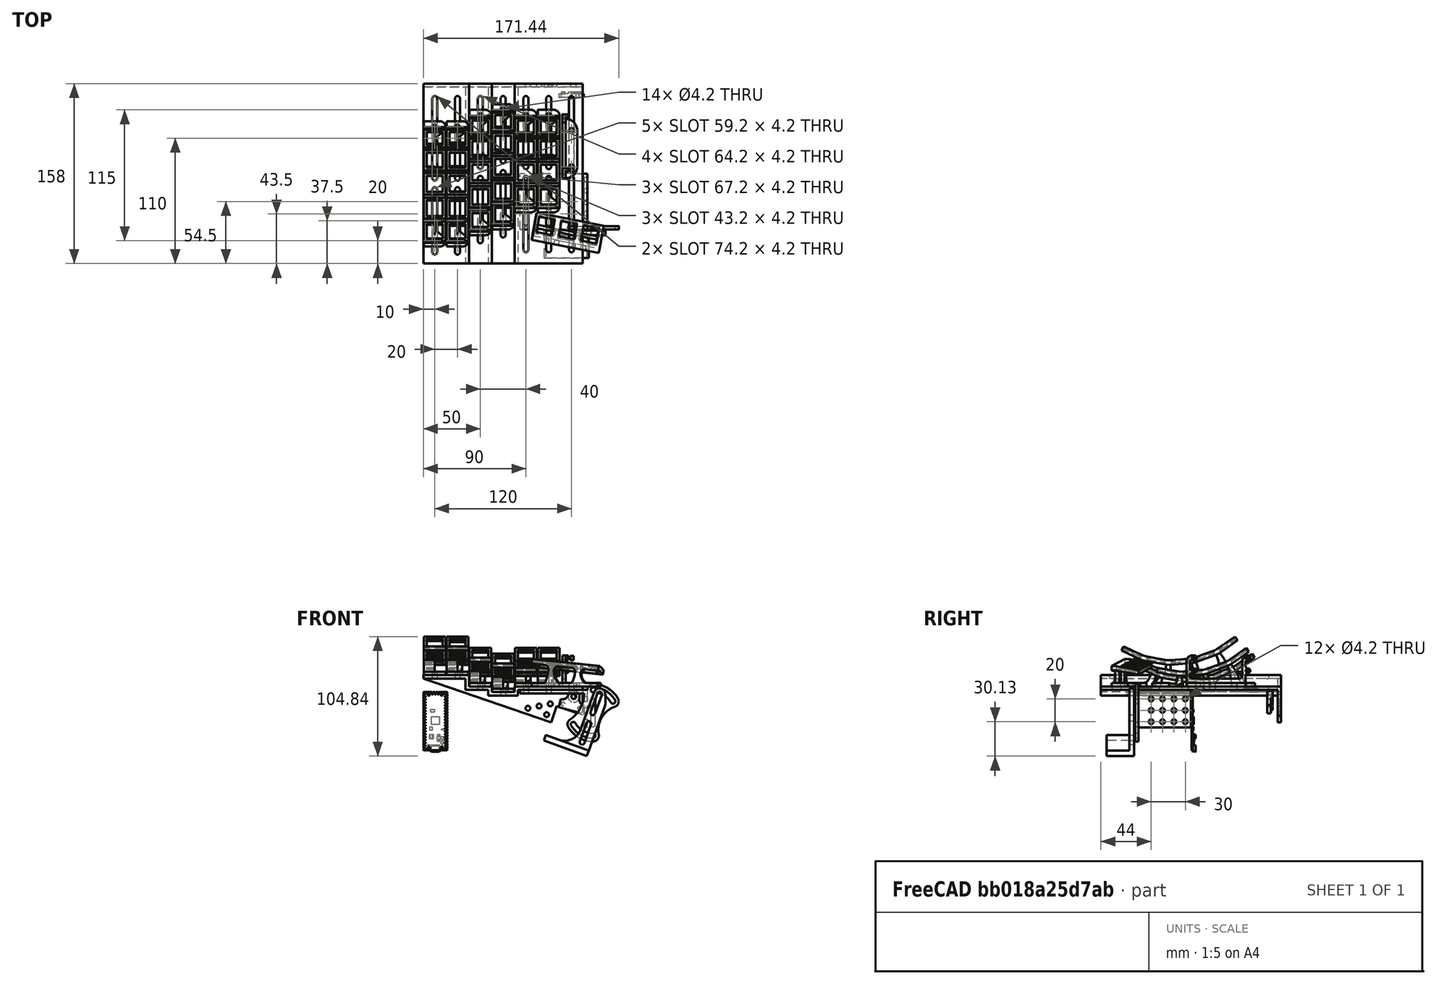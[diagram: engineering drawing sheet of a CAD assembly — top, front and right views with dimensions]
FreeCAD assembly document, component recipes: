
FREECAD ASSEMBLY — COMPONENT RECIPES ("Dactyl Chimera V3")

This assembly document has 15 components, labeled P0..P14 below (a component is one placed body or linked part). 14 of them carry a construction recipe — the FreeCAD feature program that regenerates the part from scratch, quoted from this document or its linked companion documents; the rest are supplied as boundary geometry only. No exploded tour is included for this assembly.
NOTE — this tour is split across 4 documents so each fits a 32k-token context. This is document 1: the component sections continue in the remaining 3 documents, each repeating the header above.
COMPONENT P0 — recipe-attached ("OuterArch", modeled in this document).
Construction recipe (the document's own serialized feature program — sketch geometry with constraints, then the solid features built on it; lengths are millimeters unless a unit is written):

FEATURE [Sketcher::SketchObject] Sketch
  FullyConstrained = true
  MapMode = 5
  Placement = pos=(0,0,0) rot=(0.57735,0.57735,0.57735;2.0944rad)
  Support = -> [YZ_Plane]
  expr: Constraints[147] = <<Spreadsheet>>.ARowKey
  expr: Constraints[148] = <<Spreadsheet>>.ZRowKey
  expr: Constraints[155] = <<Spreadsheet>>.QRowKey
  expr: Constraints[159] = <<Spreadsheet>>.ModRowKey
  expr: Constraints[165] = <<Spreadsheet>>.TopRowKey
  expr: Constraints[171] = <<Spreadsheet>>.Wiring
  sketch-geometry (61):
    g0: LineSegment StartX=-50 StartY=9 StartZ=0 EndX=-50 EndY=3 EndZ=0
    g1: LineSegment StartX=-9.46385 StartY=12.9848 StartZ=0 EndX=0 EndY=13.8128 EndZ=0
    g2: LineSegment StartX=0 StartY=13.8128 StartZ=0 EndX=9.46385 EndY=14.6407 EndZ=0
    g3: LineSegment StartX=9.46385 StartY=14.6407 StartZ=0 EndX=11.8732 EndY=15.1749 EndZ=0
    g4: LineSegment StartX=11.8732 StartY=15.1749 StartZ=0 EndX=20.8002 EndY=18.4241 EndZ=0
    g5: LineSegment StartX=20.8002 StartY=18.4241 StartZ=0 EndX=29.7273 EndY=21.6733 EndZ=0
    g6: LineSegment StartX=29.7273 StartY=21.6733 StartZ=0 EndX=31.9163 EndY=22.8128 EndZ=0
    g7: LineSegment StartX=31.9163 StartY=22.8128 StartZ=0 EndX=39.6982 EndY=28.2617 EndZ=0
    g8: LineSegment StartX=39.6982 StartY=28.2617 StartZ=0 EndX=47.4802 EndY=33.7107 EndZ=0
    g9: LineSegment StartX=47.4802 StartY=33.7107 StartZ=0 EndX=49.7745 EndY=30.4341 EndZ=0
    g10: LineSegment StartX=49.7745 StartY=30.4341 StartZ=0 EndX=34.2106 EndY=19.5362 EndZ=0
    g11: LineSegment StartX=34.2106 StartY=19.5362 StartZ=0 EndX=31.0954 EndY=17.9145 EndZ=0
    g12: LineSegment StartX=31.0954 StartY=17.9145 StartZ=0 EndX=13.2412 EndY=11.4161 EndZ=0
    g13: LineSegment StartX=13.2412 StartY=11.4161 StartZ=0 EndX=9.81247 EndY=10.656 EndZ=0
    g14: LineSegment StartX=9.81247 StartY=10.656 StartZ=0 EndX=-9.11523 EndY=9 EndZ=0
    g15: LineSegment StartX=-9.11523 StartY=9 StartZ=0 EndX=-12.6239 EndY=9.15319 EndZ=0
    g16: LineSegment StartX=-12.6239 StartY=9.15319 StartZ=0 EndX=-31.3353 EndY=12.4525 EndZ=0
    g17: LineSegment StartX=-31.3353 StartY=12.4525 StartZ=0 EndX=-34.6847 EndY=13.5086 EndZ=0
    g18: LineSegment StartX=-34.6847 StartY=13.5086 StartZ=0 EndX=-51.9046 EndY=21.5383 EndZ=0
    g19: LineSegment StartX=-51.9046 StartY=21.5383 StartZ=0 EndX=-50.2141 EndY=25.1636 EndZ=0
    g20: LineSegment StartX=-50.2141 StartY=25.1636 StartZ=0 EndX=-41.6042 EndY=21.1487 EndZ=0
    g21: LineSegment StartX=-41.6042 StartY=21.1487 StartZ=0 EndX=-32.9942 EndY=17.1338 EndZ=0
    g22: LineSegment StartX=-32.9942 StartY=17.1338 StartZ=0 EndX=-30.6407 EndY=16.3917 EndZ=0
    g23: LineSegment StartX=-30.6407 StartY=16.3917 StartZ=0 EndX=-21.285 EndY=14.7421 EndZ=0
    g24: LineSegment StartX=-21.285 StartY=14.7421 StartZ=0 EndX=-11.9293 EndY=13.0924 EndZ=0
    g25: LineSegment StartX=-11.9293 StartY=13.0924 StartZ=0 EndX=-9.46385 EndY=12.9848 EndZ=0
    g26: LineSegment StartX=-34.6847 StartY=13.5086 StartZ=0 EndX=-32.9942 EndY=17.1338 EndZ=0
    g27: LineSegment StartX=-30.6407 StartY=16.3917 StartZ=0 EndX=-31.3353 EndY=12.4525 EndZ=0
    g28: LineSegment StartX=-12.6239 StartY=9.15319 StartZ=0 EndX=-11.9293 EndY=13.0924 EndZ=0
    g29: LineSegment StartX=-9.46385 StartY=12.9848 StartZ=0 EndX=-9.11523 EndY=9 EndZ=0
    g30: LineSegment StartX=9.46385 StartY=14.6407 StartZ=0 EndX=9.81247 EndY=10.656 EndZ=0
    g31: LineSegment StartX=11.8732 StartY=15.1749 StartZ=0 EndX=13.2412 EndY=11.4161 EndZ=0
    g32: LineSegment StartX=29.7273 StartY=21.6733 StartZ=0 EndX=31.0954 EndY=17.9145 EndZ=0
    g33: LineSegment StartX=31.9163 StartY=22.8128 StartZ=0 EndX=34.2106 EndY=19.5362 EndZ=0
    g34: LineSegment StartX=-41.6042 StartY=21.1487 StartZ=0 EndX=-39.4911 EndY=25.6802 EndZ=0
    g35: LineSegment StartX=-21.285 StartY=14.7421 StartZ=0 EndX=-20.4167 EndY=19.6661 EndZ=0
    g36: LineSegment StartX=0 StartY=13.8128 StartZ=0 EndX=-0.435779 EndY=18.7937 EndZ=0
    g37: LineSegment StartX=20.8002 StartY=18.4241 StartZ=0 EndX=19.0901 EndY=23.1225 EndZ=0
    g38: LineSegment StartX=39.6982 StartY=28.2617 StartZ=0 EndX=36.8304 EndY=32.3575 EndZ=0
    g39: LineSegment StartX=-39.4911 StartY=25.6802 StartZ=0 EndX=-36.7722 EndY=24.4124 EndZ=0
    g40: LineSegment StartX=-36.7722 StartY=24.4124 StartZ=0 EndX=-32.546 EndY=33.4755 EndZ=0
    g41: LineSegment StartX=-21.6347 StartY=30.0351 StartZ=0 EndX=-23.3712 EndY=20.1871 EndZ=0
    g42: LineSegment StartX=-23.3712 StartY=20.1871 StartZ=0 EndX=-20.4167 EndY=19.6661 EndZ=0
    g43: LineSegment StartX=-20.4167 StartY=19.6661 StartZ=0 EndX=-17.4623 EndY=19.1452 EndZ=0
    g44: LineSegment StartX=-17.4623 StartY=19.1452 StartZ=0 EndX=-15.7258 EndY=28.9933 EndZ=0
    g45: LineSegment StartX=-4.29592 StartY=28.4942 StartZ=0 EndX=-3.42436 EndY=18.5323 EndZ=0
    g46: LineSegment StartX=-3.42436 StartY=18.5323 StartZ=0 EndX=-0.435779 EndY=18.7937 EndZ=0
    g47: LineSegment StartX=-0.435779 StartY=18.7937 StartZ=0 EndX=2.55281 EndY=19.0552 EndZ=0
    g48: LineSegment StartX=2.55281 StartY=19.0552 StartZ=0 EndX=1.68125 EndY=29.0171 EndZ=0
    g49: LineSegment StartX=12.8509 StartY=31.4934 StartZ=0 EndX=16.2711 EndY=22.0965 EndZ=0
    g50: LineSegment StartX=16.2711 StartY=22.0965 StartZ=0 EndX=19.0901 EndY=23.1225 EndZ=0
    g51: LineSegment StartX=19.0901 StartY=23.1225 StartZ=0 EndX=21.9092 EndY=24.1486 EndZ=0
    g52: LineSegment StartX=21.9092 StartY=24.1486 StartZ=0 EndX=18.489 EndY=33.5455 EndZ=0
    g53: LineSegment StartX=28.6371 StartY=38.8283 StartZ=0 EndX=34.3729 EndY=30.6368 EndZ=0
    g54: LineSegment StartX=34.3729 StartY=30.6368 StartZ=0 EndX=36.8304 EndY=32.3575 EndZ=0
    g55: ArcOfCircle CenterX=-14.0244 CenterY=73.195 CenterZ=0 NormalX=0 NormalY=0 NormalZ=1 AngleXU=0 Radius=43.8257 StartAngle=4.27606 EndAngle=4.53786
    g56: ArcOfCircle CenterX=-8.11558 CenterY=72.1532 CenterZ=0 NormalX=0 NormalY=0 NormalZ=1 AngleXU=0 Radius=43.8257 StartAngle=4.53786 EndAngle=4.79966
    g57: ArcOfCircle CenterX=-2.13841 CenterY=72.6761 CenterZ=0 NormalX=0 NormalY=0 NormalZ=1 AngleXU=0 Radius=43.8257 StartAngle=4.79966 EndAngle=5.06145
    g58: ArcOfCircle CenterX=3.49974 CenterY=74.7282 CenterZ=0 NormalX=0 NormalY=0 NormalZ=1 AngleXU=0 Radius=43.8257 StartAngle=5.06145 EndAngle=5.32325
    g59: LineSegment StartX=-50 StartY=9 StartZ=0 EndX=-70 EndY=9 EndZ=0
    g60: LineSegment StartX=-50 StartY=9 StartZ=0 EndX=50 EndY=9 EndZ=0
  constraints (176):
    c: Vertical(g0)
    c: Coincident(g1,g2)
    c: Coincident(g2,g3)
    c: Coincident(g3,g4)
    c: Coincident(g4,g5)
    c: Coincident(g5,g6)
    c: Coincident(g6,g7)
    c: Coincident(g7,g8)
    c: Coincident(g8,g9)
    c: Coincident(g9,g10)
    c: Coincident(g10,g11)
    c: Coincident(g11,g12)
    c: Coincident(g12,g13)
    c: Coincident(g13,g14)
    c: Coincident(g14,g15)
    c: Coincident(g15,g16)
    c: Coincident(g16,g17)
    c: Coincident(g17,g18)
    c: Coincident(g18,g19)
    c: Coincident(g19,g20)
    c: Coincident(g20,g21)
    c: Coincident(g21,g22)
    c: Coincident(g22,g23)
    c: Coincident(g23,g24)
    c: Coincident(g24,g25)
    c: Coincident(g25,g1)
    c: Coincident(g26,g17)
    c: Coincident(g26,g21)
    c: Coincident(g27,g22)
    c: Coincident(g27,g16)
    c: Coincident(g28,g15)
    c: Coincident(g28,g24)
    c: Coincident(g29,g1)
    c: Coincident(g29,g14)
    c: Coincident(g30,g2)
    c: Coincident(g30,g13)
    c: Coincident(g31,g3)
    c: Coincident(g31,g12)
    c: Coincident(g32,g5)
    c: Coincident(g32,g11)
    c: Coincident(g33,g6)
    c: Coincident(g33,g10)
    c: Coincident(g34,g20)
    c: Coincident(g35,g23)
    c: Coincident(g36,g1)
    c: Coincident(g37,g4)
    c: Coincident(g38,g7)
    c: Parallel(g1,g2)
    c: Parallel(g4,g5)
    c: Parallel(g8,g7)
    c: Parallel(g21,g20)
    c: Parallel(g23,g24)
    c: Equal(g5,g4)
    c: Equal(g7,g8)
    c: Equal(g2,g1)
    c: Equal(g24,g23)
    c: Equal(g21,g20)
    c: Equal(g14,g16)
    c: Equal(g14,g12)
    c: Equal(g14,g10)
    c: Equal(g14,g18)
    c: Perpendicular(g26,g21)
    c: Perpendicular(g18,g26)
    c: Perpendicular(g19,g18)
    c: Perpendicular(g28,g24)
    c: Perpendicular(g16,g28)
    c: Perpendicular(g27,g16)
    c: Perpendicular(g14,g30)
    c: Perpendicular(g29,g14)
    c: Perpendicular(g31,g4)
    c: Perpendicular(g12,g31)
    c: Perpendicular(g32,g12)
    c: Perpendicular(g33,g7)
    c: Perpendicular(g10,g33)
    c: Perpendicular(g9,g10)
    c: Perpendicular(g8,g38)
    c: Perpendicular(g5,g37)
    c: Perpendicular(g1,g36)
    c: Perpendicular(g23,g35)
    c: Perpendicular(g20,g34)
    c: Equal(g29,g28)
    c: Equal(g27,g26)
    c: Equal(g30,g31)
    c: Equal(g32,g33)
    c: Coincident(g39,g40)
    c: Coincident(g41,g42)
    c: Coincident(g42,g35)
    c: Coincident(g42,g43)
    c: Coincident(g43,g44)
    c: Coincident(g45,g46)
    c: Coincident(g46,g36)
    c: Coincident(g46,g47)
    c: Coincident(g47,g48)
    c: Coincident(g49,g50)
    c: Coincident(g50,g37)
    c: Coincident(g50,g51)
    c: Coincident(g51,g52)
    c: Coincident(g53,g54)
    c: Coincident(g54,g38)
    c: Perpendicular(g54,g53)
    c: Perpendicular(g38,g54)
    c: Perpendicular(g51,g52)
    c: Perpendicular(g37,g51)
    c: Perpendicular(g50,g37)
    c: Perpendicular(g49,g50)
    c: Perpendicular(g47,g48)
    c: Perpendicular(g36,g47)
    c: Perpendicular(g46,g36)
    c: Perpendicular(g45,g46)
    c: Perpendicular(g43,g44)
    c: Perpendicular(g35,g43)
    c: Perpendicular(g42,g35)
    c: Perpendicular(g41,g42)
    c: Perpendicular(g39,g40)
    c: Perpendicular(g34,g39)
    c: Coincident(g55,g41)
    c: Coincident(g55,g40)
    c: Coincident(g56,g44)
    c: Coincident(g56,g45)
    c: Coincident(g57,g48)
    c: Coincident(g57,g49)
    c: Coincident(g58,g52)
    c: Coincident(g58,g53)
    c: Equal(g46,g47)
    c: Equal(g47,g50)
    c: Equal(g50,g51)
    c: Equal(g51,g54)
    c: Equal(g39,g42)
    c: Equal(g42,g43)
    c: Equal(g43,g46)
    c: Coincident(g39,g34)
    c: Distance(g14) = 19
    c: Distance(g35,g36) = 20
    c: Perpendicular(g56,g44)
    c: Perpendicular(g57,g48)
    c: Perpendicular(g57,g49)
    c: Angle(g35,g36) = 0.261799
    c: Perpendicular(g56,g45)
    c: Perpendicular(g58,g53)
    c: Perpendicular(g58,g52)
    c: Perpendicular(g55,g41)
    c: Perpendicular(g55,g40)
    c: Distance(g44) = 10
    c: Distance(g45) = 10
    c: Coincident(g59,g0)
    c: Horizontal(g59)
    c: Angle(g59,g36) = 1.65806
    c: Distance(g36) = 5
    c: Distance(g35) = 5
    c: Distance(g41) = 10
    c: Distance(g40) = 10
    c: Distance(g53) = 10
    c: Distance(g52) = 10
    c: Angle(g36,g37) = 0.261799
    c: Distance(g49) = 10
    c: Distance(g37) = 5
    c: Distance(g48) = 10
    c: Distance(g50) = 3
    c: Distance(g37,g36) = 20
    c: Distance(g34) = 5
    c: Angle(g34,g35) = 0.261799
    c: Distance(g35,g34) = 20
    c: Distance(g37,g38) = 20
    c: DistanceX(g0,g-1) = 50
    c: DistanceX(g59,g59) = 20
    c: Distance(g38) = 5
    c: Angle(g37,g38) = 0.261799
    c: Distance(g29) = 4
    c: Equal(g30,g29)
    c: Coincident(g60,g0)
    c: Horizontal(g60)
    c: DistanceY(g0,g0) = 6
    c: DistanceX(g60,g60) = 100
    c: DistanceY(g-1,g0) = 3
    c: PointOnObject(g14,g60)
    c: PointOnObject(g1,g-2)
FEATURE [PartDesign::Pad] Pad  label="OArch"
  Direction = (1,-2e-16,3e-16)
  Length = 19
  Length2 = 100
  Midplane = true
  Placement = pos=(0,0,0) rot=(0.57735,0.57735,0.57735;2.0944rad)
  Profile = -> Sketch
  Type = 0
FEATURE [Sketcher::SketchObject] Sketch001
  ExternalGeometry = -> [Pad]
  FullyConstrained = true
  MapMode = 5
  Placement = pos=(0,0,0) rot=(0.57735,0.57735,0.57735;2.0944rad)
  Support = -> [YZ_Plane]
  expr: Constraints[103] = <<Spreadsheet>>.Wiring
  expr: Constraints[104] = Spreadsheet.Wiring
  expr: Constraints[106] = <<Spreadsheet>>.Wiring
  expr: Constraints[107] = <<Spreadsheet>>.Wiring
  expr: Constraints[108] = <<Spreadsheet>>.Wiring
  expr: Constraints[109] = <<Spreadsheet>>.Wiring
  expr: Constraints[110] = <<Spreadsheet>>.Wiring
  expr: Constraints[111] = <<Spreadsheet>>.ArchLength * 2 - 10mm
  expr: Constraints[21] = <<Spreadsheet>>.ArchLength
  expr: Constraints[34] = <<Spreadsheet>>.ArchLength
  expr: Constraints[8] = <<Spreadsheet>>.Wiring + 4mm
  expr: Constraints[99] = <<Spreadsheet>>.Wiring
  sketch-geometry (44):
    g0: LineSegment StartX=-30.6407 StartY=16.3917 StartZ=0 EndX=-32.9942 EndY=17.1338 EndZ=0
    g1: LineSegment StartX=-11.9293 StartY=13.0924 StartZ=0 EndX=-9.46385 EndY=12.9848 EndZ=0
    g2: LineSegment StartX=11.8732 StartY=15.1749 StartZ=0 EndX=9.46385 EndY=14.6407 EndZ=0
    g3: LineSegment StartX=31.9163 StartY=22.8128 StartZ=0 EndX=29.7273 EndY=21.6733 EndZ=0
    g4: LineSegment StartX=-30.6407 StartY=16.3917 StartZ=0 EndX=-32.3771 EndY=6.54366 EndZ=0
    g5: LineSegment StartX=-11.9293 StartY=13.0924 StartZ=0 EndX=-13.6658 EndY=3.24435 EndZ=0
    g6: LineSegment StartX=-9.46385 StartY=12.9848 StartZ=0 EndX=-8.59229 EndY=3.02283 EndZ=0
    g7: LineSegment StartX=10.3354 StartY=4.67879 StartZ=0 EndX=9.46385 EndY=14.6407 EndZ=0
    g8: LineSegment StartX=11.8732 StartY=15.1749 StartZ=0 EndX=15.2934 EndY=5.77795 EndZ=0
    g9: LineSegment StartX=33.1475 StartY=12.2763 StartZ=0 EndX=29.7273 EndY=21.6733 EndZ=0
    g10: LineSegment StartX=31.9163 StartY=22.8128 StartZ=0 EndX=37.6521 EndY=14.6213 EndZ=0
    g11: LineSegment StartX=-37.2204 StartY=8.07075 StartZ=0 EndX=-32.9942 EndY=17.1338 EndZ=0
    g12: LineSegment StartX=-13.6658 StartY=0 StartZ=0 EndX=-8.59229 EndY=0 EndZ=0
    g13: LineSegment StartX=-45 StartY=3 StartZ=0 EndX=-45 EndY=0 EndZ=0
    g14: LineSegment StartX=-45 StartY=0 StartZ=0 EndX=-35 EndY=0 EndZ=0
    g15: LineSegment StartX=35 StartY=0 StartZ=0 EndX=45 EndY=0 EndZ=0
    g16: LineSegment StartX=45 StartY=3 StartZ=0 EndX=45 EndY=0 EndZ=0
    g17: LineSegment StartX=10.3354 StartY=0 StartZ=0 EndX=15.2934 EndY=0 EndZ=0
    g18: LineSegment StartX=-32.3771 StartY=6.54366 StartZ=0 EndX=-35 EndY=0 EndZ=0
    g19: LineSegment StartX=35 StartY=0 StartZ=0 EndX=33.1475 EndY=12.2763 EndZ=0
    g20-g23: Circle x4 (B-spline internal-alignment scaffolding for g24; pole/knot coordinates omitted)
    g24: BSplineCurve PolesCount=4 KnotsCount=2 Degree=3 IsPeriodic=0
    g25: GeomPoint X=-37.2204 Y=8.07075 Z=0
    g26: GeomPoint X=-45 Y=3 Z=0
    g27-g30: Circle x4 (B-spline internal-alignment scaffolding for g31; pole/knot coordinates omitted)
    g31: BSplineCurve PolesCount=4 KnotsCount=2 Degree=3 IsPeriodic=0
    g32: GeomPoint X=37.6521 Y=14.6213 Z=0
    g33: GeomPoint X=45 Y=3 Z=0
    g34: LineSegment StartX=45 StartY=3 StartZ=0 EndX=40 EndY=3 EndZ=0
    g35: LineSegment StartX=-45 StartY=3 StartZ=0 EndX=-40 EndY=3 EndZ=0
    g36: LineSegment StartX=42.2622 StartY=8.03741 StartZ=0 EndX=37.6521 EndY=14.6213 EndZ=0
    g37: LineSegment StartX=-37.2204 StartY=8.07075 StartZ=0 EndX=-39.0097 EndY=4.23371 EndZ=0
    g38: LineSegment StartX=-39.0097 StartY=0 StartZ=0 EndX=-39.0097 EndY=4.23371 EndZ=0
    g39: LineSegment StartX=42.2622 StartY=8.03741 StartZ=0 EndX=42.2622 EndY=0 EndZ=0
    g40: LineSegment StartX=-13.6658 StartY=3.24435 StartZ=0 EndX=-13.6658 EndY=0 EndZ=0
    g41: LineSegment StartX=-8.59229 StartY=3.02283 StartZ=0 EndX=-8.59229 EndY=0 EndZ=0
    g42: LineSegment StartX=10.3354 StartY=4.67879 StartZ=0 EndX=10.3354 EndY=0 EndZ=0
    g43: LineSegment StartX=15.2934 StartY=5.77795 StartZ=0 EndX=15.2934 EndY=0 EndZ=0
  constraints (107):
    c: Coincident(g-6,g2)
    c: Coincident(g2,g-6)
    c: Coincident(g0,g-10)
    c: Coincident(g0,g-10)
    c: Coincident(g1,g-7)
    c: Coincident(g1,g-7)
    c: Coincident(g-3,g3)
    c: Coincident(g3,g-3)
    c: Distance(g0,g11) = 10
    c: Coincident(g4,g0)
    c: Coincident(g5,g1)
    c: Coincident(g6,g1)
    c: Coincident(g8,g2)
    c: Coincident(g9,g3)
    c: Coincident(g10,g3)
    c: Coincident(g11,g0)
    c: Equal(g11,g4)
    c: Equal(g9,g10)
    c: Coincident(g7,g2)
    c: PointOnObject(g12,g-1)
    c: PointOnObject(g12,g-1)
    c: DistanceX(g-11,g16) = 45
    c: PointOnObject(g13,g-1)
    c: Vertical(g13)
    c: Coincident(g13,g14)
    c: Horizontal(g14)
    c: DistanceY(g13,g13) = 3
    c: PointOnObject(g17,g-1)
    c: Horizontal(g15)
    c: Coincident(g16,g15)
    c: Vertical(g16)
    c: Equal(g13,g16)
    c: PointOnObject(g15,g-1)
    c: Horizontal(g17)
    c: DistanceX(g13,g-11) = 45
    c: Coincident(g18,g4)
    c: Coincident(g18,g14)
    c: Coincident(g19,g15)
    c: Coincident(g19,g9)
    c: Coincident(g24,g11)
    c: Weight(g20) = 1
    c: Equal(g20,g21)
    c: Equal(g20,g22)
    c: Equal(g20,g23)
    c: Coincident(g24,g13)
    c: InternalAlignment(g20-g23 -> g24) x4
    c: InternalAlignment(g25,g24)
    c: InternalAlignment(g26,g24)
    c: Coincident(g31,g10)
    c: Weight(g27) = 1
    c: Equal(g27,g28)
    c: Equal(g27,g29)
    c: Equal(g27,g30)
    c: Coincident(g31,g16)
    c: InternalAlignment(g27-g30 -> g31) x4
    c: InternalAlignment(g32,g31)
    c: InternalAlignment(g33,g31)
    c: Coincident(g34,g29)
    c: Coincident(g35,g13)
    c: Coincident(g35,g22)
    c: Coincident(g36,g28)
    c: Coincident(g36,g10)
    c: Coincident(g37,g11)
    c: Coincident(g37,g21)
    c: PointOnObject(g38,g-1)
    c: Coincident(g38,g21)
    c: Equal(g37,g38)
    c: Parallel(g37,g11)
    c: DistanceX(g35,g35) = 5
    c: Coincident(g34,g16)
    c: Equal(g34,g35)
    c: Coincident(g39,g28)
    c: PointOnObject(g39,g-1)
    c: Equal(g36,g39)
    c: Parallel(g36,g10)
    c: Vertical(g38)
    c: Vertical(g39)
    c: Equal(g15,g14)
    c: DistanceX(g14,g14) = 10
    c: Distance(g10) = 10
    c: Equal(g9,g4)
    c: Coincident(g40,g5)
    c: Coincident(g40,g12)
    c: Coincident(g41,g6)
    c: Coincident(g41,g12)
    c: Vertical(g41)
    c: Vertical(g40)
    c: Coincident(g42,g7)
    c: Coincident(g42,g17)
    c: Coincident(g43,g8)
    c: Coincident(g43,g17)
    c: Vertical(g43)
    c: Vertical(g42)
    c: Distance(g-8,g5) = 6
    c: Equal(g6,g5)
    c: Equal(g5,g7)
    c: Equal(g7,g8)
    c: Distance(g-9,g11) = 6
    c: Distance(g-9,g4) = 6
    c: Equal(g5,g11)
    c: Distance(g-5,g7) = 6
    c: Distance(g-5,g8) = 6
    c: Distance(g-4,g9) = 6
    c: Distance(g10,g-4) = 6
    c: Distance(g6,g-8) = 6
    c: DistanceX(g22,g29) = 80
    c: Horizontal(g35)
FEATURE [PartDesign::Pad] Pad001  label="OLegs"
  BaseFeature = -> Pad
  Direction = (1,-2e-16,3e-16)
  Length = 9.5
  Length2 = 100
  Placement = pos=(0,0,0) rot=(0.57735,0.57735,0.57735;2.0944rad)
  Profile = -> Sketch001
  Reversed = true
  Type = 0
FEATURE [Sketcher::SketchObject] Sketch002
  ExternalGeometry = -> [Sketch001]
  FullyConstrained = true
  MapMode = 5
  Support = -> [XY_Plane]
  expr: Constraints[14] = <<Spreadsheet>>.NutR
  expr: Constraints[15] = <<Spreadsheet>>.NutR
  expr: Constraints[26] = <<Spreadsheet>>.ScrewD
  expr: Constraints[27] = <<Spreadsheet>>.NutR
  expr: Constraints[28] = Spreadsheet.NutR
  expr: Constraints[8] = <<Spreadsheet>>.ScrewD
  sketch-geometry (22):
    g0: LineSegment StartX=-1e-14 StartY=-45 StartZ=0 EndX=-9.5 EndY=-45 EndZ=0
    g1: LineSegment StartX=-9.5 StartY=-45 StartZ=0 EndX=-9.5 EndY=-55 EndZ=0
    g2: LineSegment StartX=-9.5 StartY=-55 StartZ=0 EndX=4.5 EndY=-55 EndZ=0
    g3: LineSegment StartX=-1e-14 StartY=-45 StartZ=0 EndX=-1e-14 EndY=-40 EndZ=0
    g4: Circle CenterX=0 CenterY=-50 CenterZ=0 NormalX=0 NormalY=0 NormalZ=1 AngleXU=0 Radius=2.1
    g5: ArcOfCircle CenterX=4.5 CenterY=-50 CenterZ=0 NormalX=0 NormalY=0 NormalZ=1 AngleXU=0 Radius=5 StartAngle=4.71239 EndAngle=7.17949
    g6: LineSegment StartX=0 StartY=-50 StartZ=0 EndX=4.5 EndY=-50 EndZ=0
    g7: LineSegment StartX=9.8e-15 StartY=40 StartZ=0 EndX=9.8e-15 EndY=45 EndZ=0
    g8: LineSegment StartX=9.8e-15 StartY=45 StartZ=0 EndX=-9.5 EndY=45 EndZ=0
    g9: LineSegment StartX=-9.5 StartY=45 StartZ=0 EndX=-9.5 EndY=55 EndZ=0
    g10: LineSegment StartX=-9.5 StartY=55 StartZ=0 EndX=4.5 EndY=55 EndZ=0
    g11: ArcOfCircle CenterX=4.5 CenterY=50 CenterZ=0 NormalX=0 NormalY=0 NormalZ=1 AngleXU=0 Radius=5 StartAngle=5.38688 EndAngle=7.85398
    g12: Circle CenterX=0 CenterY=50 CenterZ=0 NormalX=0 NormalY=0 NormalZ=1 AngleXU=0 Radius=2.1
    g13: LineSegment StartX=0 StartY=50 StartZ=0 EndX=4.5 EndY=50 EndZ=0
    g14: LineSegment StartX=7.6225 StartY=46.0949 StartZ=0 EndX=9.8e-15 EndY=40 EndZ=0
    g15: LineSegment StartX=-1e-14 StartY=-40 StartZ=0 EndX=7.6225 EndY=-46.0949 EndZ=0
    g16: LineSegment StartX=9.5 StartY=55 StartZ=0 EndX=9.5 EndY=50 EndZ=0
    g17: LineSegment StartX=-9.5 StartY=55 StartZ=0 EndX=0 EndY=50 EndZ=0
    g18: LineSegment StartX=9.5 StartY=55 StartZ=0 EndX=0 EndY=50 EndZ=0
    g19: LineSegment StartX=9.5 StartY=-50 StartZ=0 EndX=9.5 EndY=-55 EndZ=0
    g20: LineSegment StartX=9.5 StartY=-55 StartZ=0 EndX=0 EndY=-50 EndZ=0
    g21: LineSegment StartX=0 StartY=-50 StartZ=0 EndX=-9.5 EndY=-55 EndZ=0
  constraints (58):
    c: Coincident(g0,g-3)
    c: Horizontal(g0)
    c: Coincident(g1,g0)
    c: Vertical(g1)
    c: Coincident(g2,g1)
    c: Horizontal(g2)
    c: Coincident(g3,g0)
    c: DistanceY(g3,g3) = 5
    c: Diameter(g4) = 4.2
    c: Tangent(g5,g2) = -1.5708
    c: Coincident(g6,g4)
    c: Coincident(g6,g5)
    c: Horizontal(g6)
    c: PointOnObject(g4,g-2)
    c: DistanceY(g4,g0) = 5
    c: DistanceY(g1,g4) = 5
    c: Vertical(g7)
    c: Coincident(g7,g8)
    c: Horizontal(g8)
    c: Coincident(g8,g9)
    c: Vertical(g9)
    c: Coincident(g9,g10)
    c: Horizontal(g10)
    c: Tangent(g11,g10) = 1.5708
    c: DistanceY(g7,g7) = 5
    c: PointOnObject(g12,g-2)
    c: Diameter(g12) = 4.2
    c: DistanceY(g8,g12) = 5
    c: DistanceY(g12,g9) = 5
    c: Coincident(g13,g12)
    c: Coincident(g13,g11)
    c: Horizontal(g13)
    c: Coincident(g14,g7)
    c: Vertical(g3)
    c: Coincident(g15,g3)
    c: Coincident(g7,g-4)
    c: Tangent(g14,g11) = 1.5708
    c: Vertical(g16)
    c: Tangent(g16,g11)
    c: PointOnObject(g16,g11)
    c: Horizontal(g16,g10)
    c: DistanceX(g9,g16) = 19
    c: Coincident(g17,g9)
    c: Coincident(g17,g12)
    c: Coincident(g18,g16)
    c: Coincident(g18,g12)
    c: Equal(g18,g17)
    c: Tangent(g15,g5) = 1.5708
    c: Vertical(g19)
    c: Tangent(g19,g5)
    c: Coincident(g19,g20)
    c: Coincident(g20,g4)
    c: Coincident(g20,g21)
    c: Coincident(g21,g1)
    c: Horizontal(g19,g2)
    c: PointOnObject(g19,g5)
    c: Equal(g20,g21)
    c: DistanceX(g1,g19) = 19
FEATURE [PartDesign::Pad] Pad002  label="OFeet"
  BaseFeature = -> Pad001
  Direction = (0,0,1)
  Length = 3
  Length2 = 100
  Placement = pos=(0,0,0) rot=(0.57735,0.57735,0.57735;2.0944rad)
  Profile = -> Sketch002
  Type = 0
FEATURE [Sketcher::SketchObject] Sketch003
  ExternalGeometry = -> [Sketch]
  FullyConstrained = true
  MapMode = 5
  Placement = pos=(0,0,0) rot=(0.57735,0.57735,0.57735;2.0944rad)
  Support = -> [YZ_Plane]
  sketch-geometry (75):
    g0: LineSegment StartX=-41.6042 StartY=21.1487 StartZ=0 EndX=-47.9483 EndY=24.107 EndZ=0
    g1: LineSegment StartX=-41.6042 StartY=21.1487 StartZ=0 EndX=-35.26 EndY=18.1904 EndZ=0
    g2: LineSegment StartX=-41.6042 StartY=21.1487 StartZ=0 EndX=-43.2946 EndY=17.5235 EndZ=0
    g3: LineSegment StartX=-35.7723 StartY=14.0157 StartZ=0 EndX=-43.2946 EndY=17.5235 EndZ=0
    g4: LineSegment StartX=-43.2946 StartY=17.5235 StartZ=0 EndX=-50.817 EndY=21.0312 EndZ=0
    g5: LineSegment StartX=-50.817 StartY=21.0312 StartZ=0 EndX=-49.7182 EndY=23.3876 EndZ=0
    g6: LineSegment StartX=-47.9483 StartY=24.107 StartZ=0 EndX=-49.6388 EndY=20.4818 EndZ=0
    g7: LineSegment StartX=-49.7182 StartY=23.3876 StartZ=0 EndX=-48.54 EndY=22.8382 EndZ=0
    g8: LineSegment StartX=-48.54 StartY=22.8382 StartZ=0 EndX=-47.9483 EndY=24.107 EndZ=0
    g9: LineSegment StartX=-35.26 StartY=18.1904 StartZ=0 EndX=-35.8517 EndY=16.9215 EndZ=0
    g10: LineSegment StartX=-35.8517 StartY=16.9215 StartZ=0 EndX=-34.6735 EndY=16.3721 EndZ=0
    g11: LineSegment StartX=-35.7723 StartY=14.0157 StartZ=0 EndX=-34.6735 EndY=16.3721 EndZ=0
    g12: LineSegment StartX=-35.26 StartY=18.1904 StartZ=0 EndX=-36.9505 EndY=14.5651 EndZ=0
    g13: LineSegment StartX=-35.7723 StartY=14.0157 StartZ=0 EndX=-34.0818 EndY=17.641 EndZ=0
    g14: LineSegment StartX=-21.285 StartY=14.7421 StartZ=0 EndX=-21.9796 EndY=10.8028 EndZ=0
    g15: LineSegment StartX=0 StartY=13.8128 StartZ=0 EndX=0.348623 EndY=9.82798 EndZ=0
    g16: LineSegment StartX=20.8002 StartY=18.4241 StartZ=0 EndX=22.1683 EndY=14.6653 EndZ=0
    g17: LineSegment StartX=39.6982 StartY=28.2617 StartZ=0 EndX=41.9925 EndY=24.9851 EndZ=0
    g18: LineSegment StartX=-28.1786 StartY=15.9576 StartZ=0 EndX=-21.285 EndY=14.7421 EndZ=0
    g19: LineSegment StartX=-21.285 StartY=14.7421 StartZ=0 EndX=-14.3913 EndY=13.5265 EndZ=0
    g20: LineSegment StartX=-6.97336 StartY=13.2027 StartZ=0 EndX=0 EndY=13.8128 EndZ=0
    g21: LineSegment StartX=0 StartY=13.8128 StartZ=0 EndX=6.97336 EndY=14.4228 EndZ=0
    g22: LineSegment StartX=14.2224 StartY=16.0299 StartZ=0 EndX=20.8002 EndY=18.4241 EndZ=0
    g23: LineSegment StartX=20.8002 StartY=18.4241 StartZ=0 EndX=27.3781 EndY=20.8182 EndZ=0
    g24: LineSegment StartX=33.9642 StartY=24.2467 StartZ=0 EndX=39.6982 EndY=28.2617 EndZ=0
    g25: LineSegment StartX=39.6982 StartY=28.2617 StartZ=0 EndX=45.4323 EndY=32.2768 EndZ=0
    g26: LineSegment StartX=-30.1535 StartY=12.2441 StartZ=0 EndX=-21.9796 EndY=10.8028 EndZ=0
    g27: LineSegment StartX=-21.9796 StartY=10.8028 StartZ=0 EndX=-13.8057 EndY=9.36157 EndZ=0
    g28: LineSegment StartX=-7.91979 StartY=9.10459 StartZ=0 EndX=0.348623 EndY=9.82798 EndZ=0
    g29: LineSegment StartX=0.348623 StartY=9.82798 StartZ=0 EndX=8.61704 EndY=10.5514 EndZ=0
    g30: LineSegment StartX=14.3689 StartY=11.8265 StartZ=0 EndX=22.1683 EndY=14.6653 EndZ=0
    g31: LineSegment StartX=22.1683 StartY=14.6653 StartZ=0 EndX=29.9678 EndY=17.5041 EndZ=0
    g32: LineSegment StartX=-28.1786 StartY=15.9576 StartZ=0 EndX=-28.8732 EndY=12.0184 EndZ=0
    g33: LineSegment StartX=-14.3913 StartY=13.5265 StartZ=0 EndX=-15.0859 EndY=9.58731 EndZ=0
    g34: LineSegment StartX=-13.8057 StartY=9.36157 StartZ=0 EndX=-13.1111 EndY=13.3008 EndZ=0
    g35: LineSegment StartX=-6.97336 StartY=13.2027 StartZ=0 EndX=-6.62474 EndY=9.21789 EndZ=0
    g36: LineSegment StartX=-7.91979 StartY=9.10459 StartZ=0 EndX=-8.26842 EndY=13.0894 EndZ=0
    g37: LineSegment StartX=6.97336 StartY=14.4228 StartZ=0 EndX=7.32199 EndY=10.4381 EndZ=0
    g38: LineSegment StartX=8.61704 StartY=10.5514 StartZ=0 EndX=8.26842 EndY=14.5362 EndZ=0
    g39: LineSegment StartX=14.3689 StartY=11.8265 StartZ=0 EndX=13.0008 EndY=15.5853 EndZ=0
    g40: LineSegment StartX=14.2224 StartY=16.0299 StartZ=0 EndX=15.5905 EndY=12.2711 EndZ=0
    g41: LineSegment StartX=27.3781 StartY=20.8182 StartZ=0 EndX=28.7462 EndY=17.0594 EndZ=0
    g42: LineSegment StartX=29.9678 StartY=17.5041 StartZ=0 EndX=28.5997 EndY=21.2628 EndZ=0
    g43: LineSegment StartX=35.1936 StartY=20.2244 StartZ=0 EndX=32.8993 EndY=23.5011 EndZ=0
    g44: LineSegment StartX=33.9642 StartY=24.2467 StartZ=0 EndX=36.2585 EndY=20.9701 EndZ=0
    g45: LineSegment StartX=45.4323 StartY=32.2768 StartZ=0 EndX=47.7266 EndY=29.0002 EndZ=0
    g46: LineSegment StartX=48.7915 StartY=29.7458 StartZ=0 EndX=46.4972 EndY=33.0224 EndZ=0
    g47: LineSegment StartX=-30.1535 StartY=12.2441 StartZ=0 EndX=-29.4589 EndY=16.1834 EndZ=0
    g48: LineSegment StartX=-30.1535 StartY=12.2441 StartZ=0 EndX=-29.702 EndY=14.8046 EndZ=0
    g49: LineSegment StartX=-29.702 StartY=14.8046 StartZ=0 EndX=-28.4218 EndY=14.5789 EndZ=0
    g50: LineSegment StartX=-28.4218 StartY=14.5789 StartZ=0 EndX=-28.1786 EndY=15.9576 EndZ=0
    g51: LineSegment StartX=-13.8057 StartY=9.36157 StartZ=0 EndX=-13.3542 EndY=11.9221 EndZ=0
    g52: LineSegment StartX=-13.3542 StartY=11.9221 StartZ=0 EndX=-14.6344 EndY=12.1478 EndZ=0
    g53: LineSegment StartX=-14.6344 StartY=12.1478 StartZ=0 EndX=-14.3913 EndY=13.5265 EndZ=0
    g54: LineSegment StartX=-7.91979 StartY=9.10459 StartZ=0 EndX=-8.14639 EndY=11.6947 EndZ=0
    g55: LineSegment StartX=-8.14639 StartY=11.6947 StartZ=0 EndX=-6.85134 EndY=11.808 EndZ=0
    g56: LineSegment StartX=-6.85134 StartY=11.808 StartZ=0 EndX=-6.97336 EndY=13.2027 EndZ=0
    g57: LineSegment StartX=6.97336 StartY=14.4228 StartZ=0 EndX=7.09538 EndY=13.0282 EndZ=0
    g58: LineSegment StartX=7.09538 StartY=13.0282 StartZ=0 EndX=8.39044 EndY=13.1415 EndZ=0
    g59: LineSegment StartX=8.39044 StartY=13.1415 StartZ=0 EndX=8.61704 EndY=10.5514 EndZ=0
    g60: LineSegment StartX=14.3689 StartY=11.8265 StartZ=0 EndX=13.4796 EndY=14.2697 EndZ=0
    g61: LineSegment StartX=13.4796 StartY=14.2697 StartZ=0 EndX=14.7012 EndY=14.7144 EndZ=0
    g62: LineSegment StartX=14.7012 StartY=14.7144 StartZ=0 EndX=14.2224 EndY=16.0299 EndZ=0
    g63: LineSegment StartX=29.9678 StartY=17.5041 StartZ=0 EndX=29.0785 EndY=19.9473 EndZ=0
    g64: LineSegment StartX=29.0785 StartY=19.9473 StartZ=0 EndX=27.8569 EndY=19.5026 EndZ=0
    g65: LineSegment StartX=27.8569 StartY=19.5026 StartZ=0 EndX=27.3781 EndY=20.8182 EndZ=0
    g66: LineSegment StartX=35.1936 StartY=20.2244 StartZ=0 EndX=33.7023 EndY=22.3542 EndZ=0
    g67: LineSegment StartX=33.7023 StartY=22.3542 StartZ=0 EndX=34.7672 EndY=23.0999 EndZ=0
    g68: LineSegment StartX=34.7672 StartY=23.0999 StartZ=0 EndX=33.9642 EndY=24.2467 EndZ=0
    g69: LineSegment StartX=48.7915 StartY=29.7458 StartZ=0 EndX=47.3002 EndY=31.8756 EndZ=0
    g70: LineSegment StartX=47.3002 StartY=31.8756 StartZ=0 EndX=46.2353 EndY=31.13 EndZ=0
    g71: LineSegment StartX=46.2353 StartY=31.13 StartZ=0 EndX=45.4323 EndY=32.2768 EndZ=0
    g72: LineSegment StartX=-50.817 StartY=21.0312 StartZ=0 EndX=-49.1265 EndY=24.6564 EndZ=0
    g73: LineSegment StartX=48.7915 StartY=29.7458 StartZ=0 EndX=42.5661 EndY=24.166 EndZ=0
    g74: LineSegment StartX=42.5661 StartY=24.166 StartZ=0 EndX=35.1936 EndY=20.2244 EndZ=0
  constraints (216):
    c: Coincident(g0,g-10)
    c: PointOnObject(g0,g-9)
    c: Coincident(g1,g0)
    c: PointOnObject(g1,g-10)
    c: Distance(g0,g1) = 14
    c: Equal(g1,g0)
    c: Coincident(g2,g0)
    c: PointOnObject(g2,g-11)
    c: Perpendicular(g2,g0)
    c: Coincident(g3,g2)
    c: Coincident(g3,g4)
    c: PointOnObject(g4,g-11)
    c: PointOnObject(g3,g-11)
    c: Equal(g3,g4)
    c: Distance(g3,g4) = 16.6
    c: Coincident(g5,g4)
    c: Coincident(g6,g0)
    c: PointOnObject(g6,g4)
    c: Perpendicular(g0,g6)
    c: Distance(g5) = 2.6
    c: Coincident(g5,g7)
    c: Coincident(g7,g8)
    c: Coincident(g8,g0)
    c: Distance(g8) = 1.4
    c: Distance(g7,g6) = 2.6
    c: Coincident(g9,g1)
    c: Coincident(g10,g9)
    c: Coincident(g11,g3)
    c: Coincident(g10,g11)
    c: Coincident(g12,g1)
    c: PointOnObject(g12,g3)
    c: Coincident(g13,g3)
    c: PointOnObject(g13,g-10)
    c: Perpendicular(g1,g12)
    c: Perpendicular(g3,g13)
    c: Distance(g9,g12) = 2.6
    c: Distance(g10,g13) = 1.4
    c: Distance(g9) = 1.4
    c: Distance(g11) = 2.6
    c: Coincident(g14,g-13)
    c: PointOnObject(g14,g-17)
    c: Coincident(g15,g-15)
    c: PointOnObject(g15,g-16)
    c: Coincident(g16,g-5)
    c: PointOnObject(g16,g-3)
    c: Coincident(g17,g-8)
    c: PointOnObject(g17,g-6)
    c: PointOnObject(g18,g-12)
    c: Coincident(g18,g14)
    c: Coincident(g18,g19)
    c: PointOnObject(g19,g-13)
    c: PointOnObject(g20,g-14)
    c: Coincident(g20,g15)
    c: Coincident(g20,g21)
    c: PointOnObject(g21,g-15)
    c: PointOnObject(g22,g-4)
    c: Coincident(g22,g23)
    c: PointOnObject(g24,g-7)
    c: Coincident(g24,g17)
    c: Coincident(g24,g25)
    c: PointOnObject(g25,g-8)
    c: Coincident(g22,g16)
    c: PointOnObject(g23,g-5)
    c: Equal(g18,g19)
    c: Equal(g21,g20)
    c: Equal(g22,g23)
    c: Equal(g24,g25)
    c: Perpendicular(g14,g18)
    c: Perpendicular(g15,g20)
    c: Perpendicular(g22,g16)
    c: Perpendicular(g24,g17)
    c: Distance(g18,g19) = 14
    c: Distance(g20,g21) = 14
    c: Distance(g22,g23) = 14
    c: Distance(g24,g25) = 14
    c: PointOnObject(g26,g-17)
    c: Coincident(g26,g14)
    c: Coincident(g26,g27)
    c: PointOnObject(g27,g-17)
    c: PointOnObject(g28,g-16)
    c: Coincident(g28,g15)
    c: Coincident(g28,g29)
    c: PointOnObject(g29,g-16)
    c: PointOnObject(g30,g-3)
    c: Coincident(g30,g16)
    c: Coincident(g30,g31)
    c: PointOnObject(g31,g-3)
    c: PointOnObject(g46,g-6)
    c: PointOnObject(g43,g-6)
    c: Distance(g26,g27) = 16.6
    c: Equal(g27,g26)
    c: Equal(g28,g29)
    c: Equal(g30,g31)
    c: Distance(g28,g29) = 16.6
    c: Distance(g30,g31) = 16.6
    c: Distance(g43,g46) = 16.6
    c: Coincident(g32,g18)
    c: PointOnObject(g32,g26)
    c: Coincident(g33,g19)
    c: PointOnObject(g33,g27)
    c: Coincident(g34,g27)
    c: PointOnObject(g34,g-13)
    c: Coincident(g35,g20)
    c: PointOnObject(g35,g28)
    c: Coincident(g36,g28)
    c: PointOnObject(g36,g-14)
    c: Coincident(g37,g21)
    c: PointOnObject(g37,g29)
    c: Coincident(g38,g29)
    c: PointOnObject(g38,g-15)
    c: Coincident(g39,g30)
    c: PointOnObject(g39,g-4)
    c: Coincident(g41,g23)
    c: PointOnObject(g41,g31)
    c: Coincident(g42,g31)
    c: PointOnObject(g42,g-5)
    c: PointOnObject(g43,g-7)
    c: Coincident(g44,g24)
    c: Coincident(g45,g25)
    c: Coincident(g47,g26)
    c: PointOnObject(g47,g-12)
    c: Perpendicular(g26,g47)
    c: Perpendicular(g32,g18)
    c: Perpendicular(g33,g19)
    c: Perpendicular(g34,g27)
    c: Perpendicular(g28,g36)
    c: Perpendicular(g20,g35)
    c: Perpendicular(g21,g37)
    c: Perpendicular(g38,g29)
    c: Perpendicular(g30,g39)
    c: Perpendicular(g22,g40)
    c: Perpendicular(g23,g41)
    c: Perpendicular(g31,g42)
    c: Perpendicular(g24,g44)
    c: Perpendicular(g25,g45)
    c: Coincident(g26,g48)
    c: Coincident(g48,g49)
    c: Coincident(g49,g50)
    c: Coincident(g50,g18)
    c: Coincident(g27,g51)
    c: Coincident(g51,g52)
    c: Coincident(g52,g53)
    c: Coincident(g53,g19)
    c: Coincident(g54,g55)
    c: Coincident(g55,g56)
    c: Coincident(g56,g20)
    c: Coincident(g21,g57)
    c: Coincident(g57,g58)
    c: Coincident(g58,g59)
    c: Coincident(g59,g29)
    c: PointOnObject(g40,g30)
    c: Coincident(g40,g22)
    c: Coincident(g30,g60)
    c: Coincident(g60,g61)
    c: Coincident(g61,g62)
    c: Coincident(g62,g22)
    c: Coincident(g31,g63)
    c: Coincident(g63,g64)
    c: Coincident(g64,g65)
    c: Coincident(g65,g23)
    c: Coincident(g66,g67)
    c: Coincident(g67,g68)
    c: Coincident(g68,g24)
    c: Coincident(g69,g70)
    c: Coincident(g70,g71)
    c: Coincident(g71,g25)
    c: Distance(g50) = 1.4
    c: Distance(g53) = 1.4
    c: Distance(g56) = 1.4
    c: Distance(g57) = 1.4
    c: Distance(g62) = 1.4
    c: Distance(g65) = 1.4
    c: Distance(g68) = 1.4
    c: Distance(g71) = 1.4
    c: Distance(g69) = 2.6
    c: Distance(g66) = 2.6
    c: Distance(g63) = 2.6
    c: Distance(g60) = 2.6
    c: Distance(g59) = 2.6
    c: Distance(g54) = 2.6
    c: Distance(g51) = 2.6
    c: Distance(g48) = 2.6
    c: Distance(g48,g47) = 1.4
    c: Distance(g51,g34) = 1.4
    c: Distance(g54,g36) = 1.4
    c: Distance(g38,g58) = 1.4
    c: Distance(g60,g39) = 1.4
    c: Distance(g63,g42) = 1.4
    c: Distance(g66,g43) = 1.4
    c: PointOnObject(g46,g-8)
    c: Distance(g69,g46) = 1.4
    c: Distance(g70,g45) = 2.6
    c: Distance(g67,g44) = 2.6
    c: Distance(g64,g41) = 2.6
    c: Distance(g61,g40) = 2.6
    c: Distance(g57,g37) = 2.6
    c: Distance(g55,g28) = 2.6
    c: Distance(g52,g27) = 2.6
    c: Distance(g49,g26) = 2.6
    c: Coincident(g54,g28)
    c: Coincident(g72,g4)
    c: PointOnObject(g72,g-9)
    c: Distance(g5,g72) = 1.4
    c: Perpendicular(g72,g4)
    c: Coincident(g69,g73)
    c: Coincident(g73,g74)
    c: Coincident(g74,g66)
    c: Distance(g17,g73) = 1
    c: Distance(g73,g24) = 5
    c: PointOnObject(g44,g-6)
    c: Perpendicular(g-6,g43)
    c: Coincident(g66,g43)
    c: Perpendicular(g-6,g46)
    c: Coincident(g69,g46)
    c: Equal(g73,g74)
    c: PointOnObject(g45,g-6)
FEATURE [PartDesign::Pocket] Pocket  label="OMX sockets"
  BaseFeature = -> Pad002
  Direction = (-1,2e-16,-3e-16)
  Length = 14
  Length2 = 100
  Midplane = true
  Placement = pos=(0,0,0) rot=(0.57735,0.57735,0.57735;2.0944rad)
  Profile = -> Sketch003
  Type = 0
FEATURE [Sketcher::SketchObject] Sketch004
  ExternalGeometry = -> [Sketch003]
  FullyConstrained = true
  MapMode = 5
  Placement = pos=(0,0,0) rot=(0.57735,0.57735,0.57735;2.0944rad)
  Support = -> [YZ_Plane]
  sketch-geometry (40):
    g0: LineSegment StartX=-48.4555 StartY=23.0195 StartZ=0 EndX=-35.7672 EndY=17.1028 EndZ=0
    g1: LineSegment StartX=-35.7672 StartY=17.1028 StartZ=0 EndX=-35.8517 EndY=16.9215 EndZ=0
    g2: LineSegment StartX=-34.6735 StartY=16.3721 StartZ=0 EndX=-35.0116 EndY=15.6471 EndZ=0
    g3: LineSegment StartX=-35.0116 StartY=15.6471 StartZ=0 EndX=-50.0563 EndY=22.6626 EndZ=0
    g4: LineSegment StartX=-50.0563 StartY=22.6626 StartZ=0 EndX=-49.7182 EndY=23.3876 EndZ=0
    g5: LineSegment StartX=-48.54 StartY=22.8382 StartZ=0 EndX=-48.4555 EndY=23.0195 EndZ=0
    g6: LineSegment StartX=-49.7182 StartY=23.3876 StartZ=0 EndX=-48.54 EndY=22.8382 EndZ=0
    g7: LineSegment StartX=-34.6735 StartY=16.3721 StartZ=0 EndX=-35.8517 EndY=16.9215 EndZ=0
    g8: LineSegment StartX=-29.702 StartY=14.8046 StartZ=0 EndX=-29.8409 EndY=14.0168 EndZ=0
    g9: LineSegment StartX=-29.8409 StartY=14.0168 StartZ=0 EndX=-13.4931 EndY=11.1342 EndZ=0
    g10: LineSegment StartX=-13.4931 StartY=11.1342 StartZ=0 EndX=-13.3542 EndY=11.9221 EndZ=0
    g11: LineSegment StartX=-13.3542 StartY=11.9221 StartZ=0 EndX=-14.6344 EndY=12.1478 EndZ=0
    g12: LineSegment StartX=-14.6344 StartY=12.1478 StartZ=0 EndX=-14.5997 EndY=12.3448 EndZ=0
    g13: LineSegment StartX=-14.5997 StartY=12.3448 StartZ=0 EndX=-28.387 EndY=14.7759 EndZ=0
    g14: LineSegment StartX=-28.387 StartY=14.7759 StartZ=0 EndX=-28.4218 EndY=14.5789 EndZ=0
    g15: LineSegment StartX=-6.86877 StartY=12.0072 StartZ=0 EndX=-6.85134 EndY=11.808 EndZ=0
    g16: LineSegment StartX=-6.85134 StartY=11.808 StartZ=0 EndX=-8.14639 EndY=11.6947 EndZ=0
    g17: LineSegment StartX=-8.14639 StartY=11.6947 StartZ=0 EndX=-8.07666 EndY=10.8977 EndZ=0
    g18: LineSegment StartX=-8.07666 StartY=10.8977 StartZ=0 EndX=8.46017 EndY=12.3445 EndZ=0
    g19: LineSegment StartX=8.46017 StartY=12.3445 StartZ=0 EndX=8.39044 EndY=13.1415 EndZ=0
    g20: LineSegment StartX=8.39044 StartY=13.1415 StartZ=0 EndX=7.09538 EndY=13.0282 EndZ=0
    g21: LineSegment StartX=7.09538 StartY=13.0282 StartZ=0 EndX=7.07795 EndY=13.2274 EndZ=0
    g22: LineSegment StartX=7.07795 StartY=13.2274 StartZ=0 EndX=-6.86877 EndY=12.0072 EndZ=0
    g23: LineSegment StartX=14.6328 StartY=14.9023 StartZ=0 EndX=14.7012 EndY=14.7144 EndZ=0
    g24: LineSegment StartX=14.7012 StartY=14.7144 StartZ=0 EndX=13.4796 EndY=14.2697 EndZ=0
    g25: LineSegment StartX=13.4796 StartY=14.2697 StartZ=0 EndX=13.7533 EndY=13.518 EndZ=0
    g26: LineSegment StartX=13.7533 StartY=13.518 StartZ=0 EndX=29.3521 EndY=19.1955 EndZ=0
    g27: LineSegment StartX=29.3521 StartY=19.1955 StartZ=0 EndX=29.0785 EndY=19.9473 EndZ=0
    g28: LineSegment StartX=29.0785 StartY=19.9473 StartZ=0 EndX=27.8569 EndY=19.5026 EndZ=0
    g29: LineSegment StartX=27.8569 StartY=19.5026 StartZ=0 EndX=27.7885 EndY=19.6906 EndZ=0
    g30: LineSegment StartX=27.7885 StartY=19.6906 StartZ=0 EndX=14.6328 EndY=14.9023 EndZ=0
    g31: LineSegment StartX=34.7672 StartY=23.0999 StartZ=0 EndX=33.7023 EndY=22.3542 EndZ=0
    g32: LineSegment StartX=33.7023 StartY=22.3542 StartZ=0 EndX=34.1612 EndY=21.6989 EndZ=0
    g33: LineSegment StartX=34.1612 StartY=21.6989 StartZ=0 EndX=47.7591 EndY=31.2203 EndZ=0
    g34: LineSegment StartX=47.7591 StartY=31.2203 StartZ=0 EndX=47.3002 EndY=31.8756 EndZ=0
    g35: LineSegment StartX=47.3002 StartY=31.8756 StartZ=0 EndX=46.2353 EndY=31.13 EndZ=0
    g36: LineSegment StartX=46.2353 StartY=31.13 StartZ=0 EndX=46.1206 EndY=31.2938 EndZ=0
    g37: LineSegment StartX=46.1206 StartY=31.2938 StartZ=0 EndX=34.6525 EndY=23.2637 EndZ=0
    g38: LineSegment StartX=34.6525 StartY=23.2637 StartZ=0 EndX=34.7672 EndY=23.0999 EndZ=0
    g39: LineSegment StartX=-29.702 StartY=14.8046 StartZ=0 EndX=-28.4218 EndY=14.5789 EndZ=0
  constraints (100):
    c: Coincident(g0,g1)
    c: Coincident(g5,g0)
    c: Distance(g5) = 0.2
    c: Distance(g1) = 0.2
    c: Coincident(g3,g2)
    c: Coincident(g4,g3)
    c: Distance(g4) = 0.8
    c: Distance(g2) = 0.8
    c: Coincident(g6,g4)
    c: Coincident(g6,g5)
    c: Coincident(g7,g2)
    c: Coincident(g7,g1)
    c: Coincident(g8,g9)
    c: Coincident(g9,g10)
    c: Coincident(g10,g11)
    c: Coincident(g11,g12)
    c: Coincident(g12,g13)
    c: Coincident(g13,g14)
    c: Coincident(g15,g16)
    c: Coincident(g16,g17)
    c: Coincident(g17,g18)
    c: Coincident(g18,g19)
    c: Coincident(g19,g20)
    c: Coincident(g20,g21)
    c: Coincident(g21,g22)
    c: Coincident(g22,g15)
    c: Coincident(g23,g24)
    c: Coincident(g25,g26)
    c: Coincident(g26,g27)
    c: Coincident(g27,g28)
    c: Coincident(g28,g29)
    c: Coincident(g29,g30)
    c: Coincident(g30,g23)
    c: Coincident(g31,g32)
    c: Coincident(g32,g33)
    c: Coincident(g33,g34)
    c: Coincident(g35,g36)
    c: Coincident(g36,g37)
    c: Coincident(g37,g38)
    c: Coincident(g39,g8)
    c: Coincident(g39,g14)
    c: Distance(g14) = 0.2
    c: Distance(g12) = 0.2
    c: Distance(g15) = 0.2
    c: Distance(g21) = 0.2
    c: Distance(g23) = 0.2
    c: Distance(g29) = 0.2
    c: Distance(g36) = 0.2
    c: Distance(g34) = 0.8
    c: Distance(g32) = 0.8
    c: Distance(g27) = 0.8
    c: Distance(g19) = 0.8
    c: Distance(g17) = 0.8
    c: Distance(g10) = 0.8
    c: Distance(g8) = 0.8
    c: Distance(g26,g-18) = 1.8
    c: Distance(g18,g-14) = 1.8
    c: Distance(g17,g-12) = 1.8
    c: Distance(g9,g-10) = 1.8
    c: Distance(g-8,g8) = 1.8
    c: Distance(g13,g-7) = 1.2
    c: Distance(g12,g-9) = 1.2
    c: Distance(g15,g-11) = 1.2
    c: Distance(g21,g-13) = 1.2
    c: Distance(g23,g-16) = 1.2
    c: Distance(g29,g-17) = 1.2
    c: Distance(g2,g-4) = 1.8
    c: Distance(g3,g-3) = 1.8
    c: Distance(g-5,g0) = 1.2
    c: Distance(g0,g-6) = 1.2
    c: Coincident(g28,g-17)
    c: Coincident(g27,g-18)
    c: Coincident(g24,g-15)
    c: Coincident(g24,g25)
    c: Distance(g25) = 0.8
    c: Distance(g25,g-15) = 1.8
    c: Coincident(g23,g-16)
    c: Coincident(g19,g-14)
    c: Coincident(g20,g-13)
    c: Coincident(g16,g-12)
    c: Coincident(g15,g-11)
    c: Coincident(g11,g-9)
    c: Coincident(g10,g-10)
    c: Coincident(g8,g-8)
    c: Coincident(g14,g-7)
    c: Coincident(g1,g-6)
    c: Coincident(g2,g-4)
    c: Coincident(g4,g-3)
    c: Coincident(g5,g-5)
    c: Coincident(g34,g-21)
    c: Coincident(g35,g-20)
    c: Coincident(g35,g34)
    c: Distance(g33,g-21) = 1.8
    c: Distance(g36,g-20) = 1.2
    c: Distance(g38) = 0.2
    c: Distance(g37,g-22) = 1.2
    c: Coincident(g31,g-22)
    c: Coincident(g31,g-19)
    c: Distance(g32,g-19) = 1.8
    c: Coincident(g38,g31)
FEATURE [PartDesign::Pocket] Pocket001  label="OChoc sockets"
  BaseFeature = -> Pocket
  Direction = (-1,2e-16,-3e-16)
  Length = 14.6
  Length2 = 100
  Midplane = true
  Placement = pos=(0,0,0) rot=(0.57735,0.57735,0.57735;2.0944rad)
  Profile = -> Sketch004
  Type = 0
FEATURE [Sketcher::SketchObject] Sketch065
  FullyConstrained = false
  MapMode = 5
  Placement = pos=(0,0,0) rot=(1,0,0;1.5708rad)
  Support = -> [XZ_Plane]
  sketch-geometry (8):
    g0: LineSegment StartX=0 StartY=12.3824 StartZ=0 EndX=0 EndY=-3.61756 EndZ=0
    g1: LineSegment StartX=20 StartY=7.42184 StartZ=0 EndX=20 EndY=-8.57816 EndZ=0
    g2: LineSegment StartX=40 StartY=2.69316 StartZ=0 EndX=40 EndY=-13.3068 EndZ=0
    g3: LineSegment StartX=60 StartY=0.676164 StartZ=0 EndX=60 EndY=-15.3238 EndZ=0
    g4: LineSegment StartX=80 StartY=-5.67319 StartZ=0 EndX=80 EndY=-21.6732 EndZ=0
    g5: LineSegment StartX=100 StartY=-1.47822 StartZ=0 EndX=100 EndY=-17.4782 EndZ=0
    g6: LineSegment StartX=120 StartY=-1.65596 StartZ=0 EndX=120 EndY=-17.656 EndZ=0
    g7: GeomPoint X=80 Y=-13.6732 Z=0
  constraints (23):
    c: Vertical(g0)
    c: DistanceY(g0,g0) = 16
    c: PointOnObject(g0,g-2)
    c: Vertical(g1)
    c: Vertical(g2)
    c: Vertical(g3)
    c: Vertical(g4)
    c: Vertical(g5)
    c: Vertical(g6)
    c: Equal(g6,g5)
    c: Equal(g5,g4)
    c: Equal(g4,g3)
    c: Equal(g3,g2)
    c: Equal(g2,g1)
    c: Equal(g1,g0)
    c: DistanceX(g0,g1) = 20
    c: DistanceX(g1,g2) = 20
    c: DistanceX(g2,g3) = 20
    c: DistanceX(g3,g4) = 20
    c: DistanceX(g4,g5) = 20
    c: DistanceX(g5,g6) = 20
    c: PointOnObject(g7,g4)
    c: DistanceY(g4,g7) = 8
FEATURE [PartDesign::Body] Body  label="OuterArch"
  Group = -> [Sketch,Pad,Sketch001,Pad001,Sketch002,Pad002,Sketch003,Pocket,Sketch004,Pocket001,Sketch065]
  Origin = -> Origin
  Placement = pos=(10,-10,15) rot=(0,0,1;0rad)
  Tip = -> Pocket001
COMPONENT P1 — recipe-attached ("PinkieArch", modeled in this document).
Construction recipe (the document's own serialized feature program — sketch geometry with constraints, then the solid features built on it; lengths are millimeters unless a unit is written):

FEATURE [Sketcher::SketchObject] Sketch006
  FullyConstrained = true
  MapMode = 5
  Placement = pos=(0,0,0) rot=(0.57735,0.57735,0.57735;2.0944rad)
  Support = -> [YZ_Plane001]
  expr: Constraints[124] = <<Spreadsheet>>.ModRowKey
  expr: Constraints[125] = <<Spreadsheet>>.ZRowKey
  expr: Constraints[132] = <<Spreadsheet>>.ARowKey
  expr: Constraints[157] = <<Spreadsheet>>.QRowKey
  expr: Constraints[158] = <<Spreadsheet>>.TopRowKey
  expr: Constraints[169] = <<Spreadsheet>>.Wiring
  sketch-geometry (61):
    g0: LineSegment StartX=-32.9942 StartY=17.1338 StartZ=0 EndX=-30.6407 EndY=16.3917 EndZ=0
    g1: LineSegment StartX=-11.9293 StartY=13.0924 StartZ=0 EndX=-9.46385 EndY=12.9848 EndZ=0
    g2: LineSegment StartX=9.46385 StartY=14.6407 StartZ=0 EndX=11.8732 EndY=15.1749 EndZ=0
    g3: LineSegment StartX=29.7273 StartY=21.6733 StartZ=0 EndX=31.9163 EndY=22.8128 EndZ=0
    g4: LineSegment StartX=47.4802 StartY=33.7107 StartZ=0 EndX=49.7745 EndY=30.4341 EndZ=0
    g5: LineSegment StartX=49.7745 StartY=30.4341 StartZ=0 EndX=34.2106 EndY=19.5362 EndZ=0
    g6: LineSegment StartX=34.2106 StartY=19.5362 StartZ=0 EndX=31.0954 EndY=17.9145 EndZ=0
    g7: LineSegment StartX=31.0954 StartY=17.9145 StartZ=0 EndX=13.2412 EndY=11.4161 EndZ=0
    g8: LineSegment StartX=13.2412 StartY=11.4161 StartZ=0 EndX=9.81247 EndY=10.656 EndZ=0
    g9: LineSegment StartX=9.81247 StartY=10.656 StartZ=0 EndX=-9.11523 EndY=9 EndZ=0
    g10: LineSegment StartX=-9.11523 StartY=9 StartZ=0 EndX=-12.6239 EndY=9.15319 EndZ=0
    g11: LineSegment StartX=-12.6239 StartY=9.15319 StartZ=0 EndX=-31.3353 EndY=12.4525 EndZ=0
    g12: LineSegment StartX=-31.3353 StartY=12.4525 StartZ=0 EndX=-34.6847 EndY=13.5086 EndZ=0
    g13: LineSegment StartX=-34.6847 StartY=13.5086 StartZ=0 EndX=-51.9046 EndY=21.5383 EndZ=0
    g14: LineSegment StartX=-51.9046 StartY=21.5383 StartZ=0 EndX=-50.2141 EndY=25.1636 EndZ=0
    g15: LineSegment StartX=47.4802 StartY=33.7107 StartZ=0 EndX=39.6982 EndY=28.2617 EndZ=0
    g16: LineSegment StartX=39.6982 StartY=28.2617 StartZ=0 EndX=31.9163 EndY=22.8128 EndZ=0
    g17: LineSegment StartX=29.7273 StartY=21.6733 StartZ=0 EndX=20.8002 EndY=18.4241 EndZ=0
    g18: LineSegment StartX=20.8002 StartY=18.4241 StartZ=0 EndX=11.8732 EndY=15.1749 EndZ=0
    g19: LineSegment StartX=9.46385 StartY=14.6407 StartZ=0 EndX=0 EndY=13.8128 EndZ=0
    g20: LineSegment StartX=0 StartY=13.8128 StartZ=0 EndX=-9.46385 EndY=12.9848 EndZ=0
    g21: LineSegment StartX=-11.9293 StartY=13.0924 StartZ=0 EndX=-21.285 EndY=14.7421 EndZ=0
    g22: LineSegment StartX=-21.285 StartY=14.7421 StartZ=0 EndX=-30.6407 EndY=16.3917 EndZ=0
    g23: LineSegment StartX=-32.9942 StartY=17.1338 StartZ=0 EndX=-41.6042 EndY=21.1487 EndZ=0
    g24: LineSegment StartX=-41.6042 StartY=21.1487 StartZ=0 EndX=-50.2141 EndY=25.1636 EndZ=0
    g25: LineSegment StartX=-41.6042 StartY=21.1487 StartZ=0 EndX=-39.4911 EndY=25.6802 EndZ=0
    g26: LineSegment StartX=-39.4911 StartY=25.6802 StartZ=0 EndX=-36.7722 EndY=24.4124 EndZ=0
    g27: LineSegment StartX=-36.7722 StartY=24.4124 StartZ=0 EndX=-32.546 EndY=33.4755 EndZ=0
    g28: LineSegment StartX=-21.6347 StartY=30.0351 StartZ=0 EndX=-23.3712 EndY=20.1871 EndZ=0
    g29: LineSegment StartX=-23.3712 StartY=20.1871 StartZ=0 EndX=-20.4167 EndY=19.6661 EndZ=0
    g30: LineSegment StartX=-20.4167 StartY=19.6661 StartZ=0 EndX=-21.285 EndY=14.7421 EndZ=0
    g31: LineSegment StartX=-20.4167 StartY=19.6661 StartZ=0 EndX=-17.4623 EndY=19.1452 EndZ=0
    g32: LineSegment StartX=-17.4623 StartY=19.1452 StartZ=0 EndX=-15.7258 EndY=28.9933 EndZ=0
    g33: LineSegment StartX=-4.29592 StartY=28.4942 StartZ=0 EndX=-3.42436 EndY=18.5323 EndZ=0
    g34: LineSegment StartX=-3.42436 StartY=18.5323 StartZ=0 EndX=-0.435779 EndY=18.7937 EndZ=0
    g35: LineSegment StartX=-0.435779 StartY=18.7937 StartZ=0 EndX=0 EndY=13.8128 EndZ=0
    g36: LineSegment StartX=-0.435779 StartY=18.7937 StartZ=0 EndX=2.55281 EndY=19.0552 EndZ=0
    g37: LineSegment StartX=2.55281 StartY=19.0552 StartZ=0 EndX=1.68125 EndY=29.0171 EndZ=0
    g38: LineSegment StartX=12.8509 StartY=31.4934 StartZ=0 EndX=16.2711 EndY=22.0965 EndZ=0
    g39: LineSegment StartX=16.2711 StartY=22.0965 StartZ=0 EndX=19.0901 EndY=23.1225 EndZ=0
    g40: LineSegment StartX=19.0901 StartY=23.1225 StartZ=0 EndX=20.8002 EndY=18.4241 EndZ=0
    g41: LineSegment StartX=19.0901 StartY=23.1225 StartZ=0 EndX=21.9092 EndY=24.1486 EndZ=0
    g42: LineSegment StartX=21.9092 StartY=24.1486 StartZ=0 EndX=18.489 EndY=33.5455 EndZ=0
    g43: LineSegment StartX=28.6371 StartY=38.8283 StartZ=0 EndX=34.3729 EndY=30.6368 EndZ=0
    g44: LineSegment StartX=34.3729 StartY=30.6368 StartZ=0 EndX=36.8304 EndY=32.3575 EndZ=0
    g45: LineSegment StartX=36.8304 StartY=32.3575 StartZ=0 EndX=39.6982 EndY=28.2617 EndZ=0
    g46: ArcOfCircle CenterX=-14.0244 CenterY=73.195 CenterZ=0 NormalX=0 NormalY=0 NormalZ=1 AngleXU=0 Radius=43.8257 StartAngle=4.27606 EndAngle=4.53786
    g47: ArcOfCircle CenterX=-8.11558 CenterY=72.1532 CenterZ=0 NormalX=0 NormalY=0 NormalZ=1 AngleXU=0 Radius=43.8257 StartAngle=4.53786 EndAngle=4.79966
    g48: ArcOfCircle CenterX=-2.13841 CenterY=72.6761 CenterZ=0 NormalX=0 NormalY=0 NormalZ=1 AngleXU=0 Radius=43.8257 StartAngle=4.79966 EndAngle=5.06145
    g49: ArcOfCircle CenterX=3.49974 CenterY=74.7282 CenterZ=0 NormalX=0 NormalY=0 NormalZ=1 AngleXU=0 Radius=43.8257 StartAngle=5.06145 EndAngle=5.32325
    g50: LineSegment StartX=-32.9942 StartY=17.1338 StartZ=0 EndX=-34.6847 EndY=13.5086 EndZ=0
    g51: LineSegment StartX=-30.6407 StartY=16.3917 StartZ=0 EndX=-31.3353 EndY=12.4525 EndZ=0
    g52: LineSegment StartX=-12.6239 StartY=9.15319 StartZ=0 EndX=-11.9293 EndY=13.0924 EndZ=0
    g53: LineSegment StartX=-9.46385 StartY=12.9848 StartZ=0 EndX=-9.11523 EndY=9 EndZ=0
    g54: LineSegment StartX=9.46385 StartY=14.6407 StartZ=0 EndX=9.81247 EndY=10.656 EndZ=0
    g55: LineSegment StartX=11.8732 StartY=15.1749 StartZ=0 EndX=13.2412 EndY=11.4161 EndZ=0
    g56: LineSegment StartX=31.9163 StartY=22.8128 StartZ=0 EndX=34.2106 EndY=19.5362 EndZ=0
    g57: LineSegment StartX=29.7273 StartY=21.6733 StartZ=0 EndX=31.0954 EndY=17.9145 EndZ=0
    g58: LineSegment StartX=-50 StartY=3 StartZ=0 EndX=-50 EndY=9 EndZ=0
    g59: LineSegment StartX=-50 StartY=9 StartZ=0 EndX=-70 EndY=9 EndZ=0
    g60: LineSegment StartX=-50 StartY=9 StartZ=0 EndX=50 EndY=9 EndZ=0
  constraints (176):
    c: Coincident(g4,g5)
    c: Coincident(g5,g6)
    c: Coincident(g6,g7)
    c: Coincident(g7,g8)
    c: Coincident(g8,g9)
    c: Coincident(g9,g10)
    c: Coincident(g10,g11)
    c: Coincident(g11,g12)
    c: Coincident(g12,g13)
    c: Coincident(g13,g14)
    c: Coincident(g4,g15)
    c: Coincident(g15,g16)
    c: Coincident(g16,g3)
    c: Coincident(g3,g17)
    c: Coincident(g17,g18)
    c: Coincident(g18,g2)
    c: Coincident(g2,g19)
    c: Coincident(g19,g20)
    c: Coincident(g20,g1)
    c: Coincident(g1,g21)
    c: Coincident(g21,g22)
    c: Coincident(g22,g0)
    c: Coincident(g0,g23)
    c: Coincident(g23,g24)
    c: Coincident(g24,g14)
    c: Coincident(g23,g25)
    c: Coincident(g25,g26)
    c: Coincident(g26,g27)
    c: Coincident(g28,g29)
    c: Coincident(g29,g30)
    c: Coincident(g30,g21)
    c: Coincident(g29,g31)
    c: Coincident(g31,g32)
    c: Coincident(g33,g34)
    c: Coincident(g34,g35)
    c: Coincident(g35,g19)
    c: Coincident(g34,g36)
    c: Coincident(g36,g37)
    c: Coincident(g38,g39)
    c: Coincident(g39,g40)
    c: Coincident(g40,g17)
    c: Coincident(g39,g41)
    c: Coincident(g41,g42)
    c: Coincident(g43,g44)
    c: Coincident(g44,g45)
    c: Coincident(g45,g15)
    c: Coincident(g46,g27)
    c: Coincident(g46,g28)
    c: Coincident(g47,g32)
    c: Coincident(g47,g33)
    c: Coincident(g48,g37)
    c: Coincident(g48,g38)
    c: Coincident(g49,g42)
    c: Coincident(g49,g43)
    c: Distance(g9) = 19
    c: Perpendicular(g13,g14)
    c: Equal(g9,g11)
    c: Equal(g11,g13)
    c: Equal(g13,g7)
    c: Equal(g7,g5)
    c: Distance(g43) = 10
    c: Distance(g42) = 10
    c: Distance(g38) = 10
    c: Distance(g37) = 10
    c: Distance(g32) = 10
    c: Distance(g28) = 10
    c: Distance(g27) = 10
    c: Perpendicular(g46,g27)
    c: Perpendicular(g46,g28)
    c: Perpendicular(g47,g32)
    c: Perpendicular(g47,g33)
    c: Perpendicular(g48,g37)
    c: Perpendicular(g48,g38)
    c: Perpendicular(g49,g42)
    c: Perpendicular(g49,g43)
    c: Coincident(g50,g0)
    c: Coincident(g50,g12)
    c: Coincident(g51,g0)
    c: Coincident(g51,g11)
    c: Coincident(g52,g10)
    c: Coincident(g52,g1)
    c: Coincident(g53,g1)
    c: Coincident(g53,g9)
    c: Distance(g33) = 10
    c: Equal(g24,g23)
    c: Equal(g22,g21)
    c: Equal(g20,g19)
    c: Equal(g18,g17)
    c: Equal(g16,g15)
    c: Parallel(g24,g23)
    c: Parallel(g22,g21)
    c: Parallel(g20,g19)
    c: Parallel(g18,g17)
    c: Parallel(g16,g15)
    c: Coincident(g54,g2)
    c: Coincident(g54,g8)
    c: Coincident(g55,g7)
    c: Coincident(g2,g55)
    c: Coincident(g56,g3)
    c: Coincident(g56,g5)
    c: Coincident(g57,g3)
    c: Coincident(g57,g6)
    c: Perpendicular(g23,g50)
    c: Perpendicular(g13,g50)
    c: Perpendicular(g11,g51)
    c: Perpendicular(g52,g11)
    c: Perpendicular(g21,g52)
    c: Perpendicular(g53,g9)
    c: Perpendicular(g9,g54)
    c: Perpendicular(g35,g20)
    c: Equal(g54,g53)
    c: Distance(g25,g29) = 20
    c: Distance(g29,g34) = 20
    c: Distance(g34,g39) = 20
    c: Distance(g39,g44) = 20
    c: Perpendicular(g26,g27)
    c: Perpendicular(g29,g28)
    c: Perpendicular(g31,g32)
    c: Perpendicular(g36,g37)
    c: Perpendicular(g38,g39)
    c: Perpendicular(g41,g42)
    c: Perpendicular(g43,g44)
    c: Perpendicular(g24,g25)
    c: Perpendicular(g22,g30)
    c: Distance(g25) = 5
    c: Distance(g30) = 5
    c: Perpendicular(g26,g25)
    c: Perpendicular(g30,g31)
    c: Perpendicular(g30,g29)
    c: Equal(g53,g52)
    c: Equal(g50,g51)
    c: Equal(g55,g54)
    c: Distance(g35) = 5
    c: Perpendicular(g36,g35)
    c: Distance(g53) = 4
    c: Perpendicular(g34,g35)
    c: Perpendicular(g33,g34)
    c: Perpendicular(g18,g40)
    c: Equal(g57,g56)
    c: Perpendicular(g55,g7)
    c: Perpendicular(g55,g18)
    c: Perpendicular(g17,g57)
    c: Perpendicular(g40,g41)
    c: Perpendicular(g56,g5)
    c: Perpendicular(g15,g4)
    c: Perpendicular(g5,g4)
    c: Perpendicular(g16,g45)
    c: Equal(g26,g29)
    c: Equal(g31,g29)
    c: Equal(g34,g36)
    c: Equal(g31,g34)
    c: Equal(g36,g39)
    c: Perpendicular(g40,g39)
    c: Equal(g44,g41)
    c: Angle(g25,g30) = 0.261799
    c: Angle(g30,g35) = 0.261799
    c: Angle(g35,g40) = 0.261799
    c: Distance(g40) = 5
    c: Distance(g45) = 5
    c: Perpendicular(g44,g45)
    c: Angle(g40,g45) = 0.261799
    c: Vertical(g58)
    c: Coincident(g59,g58)
    c: Horizontal(g59)
    c: Coincident(g60,g58)
    c: Horizontal(g60)
    c: DistanceX(g59,g59) = 20
    c: DistanceX(g58,g-1) = 50
    c: DistanceX(g60,g60) = 100
    c: DistanceY(g58,g58) = 6
    c: DistanceY(g-1,g58) = 3
    c: Angle(g59,g35) = 1.65806
    c: Equal(g39,g41)
    c: Distance(g39) = 3
    c: PointOnObject(g19,g-2)
    c: PointOnObject(g9,g60)
FEATURE [PartDesign::Pad] Pad004  label="PArch"
  Direction = (1,-2e-16,3e-16)
  Length = 19
  Length2 = 100
  Midplane = true
  Placement = pos=(0,0,0) rot=(0.57735,0.57735,0.57735;2.0944rad)
  Profile = -> Sketch006
  Type = 0
FEATURE [Sketcher::SketchObject] Sketch007
  ExternalGeometry = -> [Sketch006]
  FullyConstrained = true
  MapMode = 5
  Placement = pos=(0,0,0) rot=(0.57735,0.57735,0.57735;2.0944rad)
  Support = -> [YZ_Plane001]
  sketch-geometry (85):
    g0: LineSegment StartX=-49.1265 StartY=24.6564 StartZ=0 EndX=-50.817 EndY=21.0312 EndZ=0
    g1: LineSegment StartX=-49.6388 StartY=20.4818 StartZ=0 EndX=-47.9483 EndY=24.107 EndZ=0
    g2: LineSegment StartX=-41.6042 StartY=21.1487 StartZ=0 EndX=-43.2946 EndY=17.5235 EndZ=0
    g3: LineSegment StartX=-35.26 StartY=18.1904 StartZ=0 EndX=-36.9505 EndY=14.5651 EndZ=0
    g4: LineSegment StartX=-35.7723 StartY=14.0157 StartZ=0 EndX=-34.0818 EndY=17.641 EndZ=0
    g5: LineSegment StartX=-29.4589 StartY=16.1834 StartZ=0 EndX=-30.1535 EndY=12.2441 EndZ=0
    g6: LineSegment StartX=-28.8732 StartY=12.0184 StartZ=0 EndX=-28.1786 EndY=15.9576 EndZ=0
    g7: LineSegment StartX=-21.285 StartY=14.7421 StartZ=0 EndX=-21.9796 EndY=10.8028 EndZ=0
    g8: LineSegment StartX=-15.0859 StartY=9.58731 StartZ=0 EndX=-14.3913 EndY=13.5265 EndZ=0
    g9: LineSegment StartX=-13.1111 StartY=13.3008 StartZ=0 EndX=-13.8057 EndY=9.36157 EndZ=0
    g10: LineSegment StartX=-8.26842 StartY=13.0894 StartZ=0 EndX=-7.91979 EndY=9.10459 EndZ=0
    g11: LineSegment StartX=-6.62474 StartY=9.21789 StartZ=0 EndX=-6.97336 EndY=13.2027 EndZ=0
    g12: LineSegment StartX=0 StartY=13.8128 StartZ=0 EndX=0.348623 EndY=9.82798 EndZ=0
    g13: LineSegment StartX=7.32199 StartY=10.4381 StartZ=0 EndX=6.97336 EndY=14.4228 EndZ=0
    g14: LineSegment StartX=8.26842 StartY=14.5362 StartZ=0 EndX=8.61704 EndY=10.5514 EndZ=0
    g15: LineSegment StartX=14.3689 StartY=11.8265 StartZ=0 EndX=13.0008 EndY=15.5853 EndZ=0
    g16: LineSegment StartX=14.2224 StartY=16.0299 StartZ=0 EndX=15.5905 EndY=12.2711 EndZ=0
    g17: LineSegment StartX=20.8002 StartY=18.4241 StartZ=0 EndX=22.1683 EndY=14.6653 EndZ=0
    g18: LineSegment StartX=28.7462 StartY=17.0594 StartZ=0 EndX=27.3781 EndY=20.8182 EndZ=0
    g19: LineSegment StartX=28.5997 StartY=21.2628 StartZ=0 EndX=29.9678 EndY=17.5041 EndZ=0
    g20: LineSegment StartX=35.1936 StartY=20.2244 StartZ=0 EndX=32.8993 EndY=23.5011 EndZ=0
    g21: LineSegment StartX=33.9642 StartY=24.2467 StartZ=0 EndX=36.2585 EndY=20.9701 EndZ=0
    g22: LineSegment StartX=39.6982 StartY=28.2617 StartZ=0 EndX=41.9925 EndY=24.9851 EndZ=0
    g23: LineSegment StartX=45.4323 StartY=32.2768 StartZ=0 EndX=47.7266 EndY=29.0002 EndZ=0
    g24: LineSegment StartX=48.7915 StartY=29.7458 StartZ=0 EndX=46.4972 EndY=33.0224 EndZ=0
    g25: LineSegment StartX=-47.9483 StartY=24.107 StartZ=0 EndX=-41.6042 EndY=21.1487 EndZ=0
    g26: LineSegment StartX=-41.6042 StartY=21.1487 StartZ=0 EndX=-35.26 EndY=18.1904 EndZ=0
    g27: LineSegment StartX=-35.26 StartY=18.1904 StartZ=0 EndX=-35.8517 EndY=16.9215 EndZ=0
    g28: LineSegment StartX=-35.8517 StartY=16.9215 StartZ=0 EndX=-34.6735 EndY=16.3721 EndZ=0
    g29: LineSegment StartX=-34.6735 StartY=16.3721 StartZ=0 EndX=-36.9505 EndY=14.5651 EndZ=0
    g30: LineSegment StartX=-49.6388 StartY=20.4818 StartZ=0 EndX=-49.7182 EndY=23.3876 EndZ=0
    g31: LineSegment StartX=-49.7182 StartY=23.3876 StartZ=0 EndX=-48.54 EndY=22.8382 EndZ=0
    g32: LineSegment StartX=-48.54 StartY=22.8382 StartZ=0 EndX=-47.9483 EndY=24.107 EndZ=0
    g33: LineSegment StartX=-29.702 StartY=14.8046 StartZ=0 EndX=-28.4217 EndY=14.5789 EndZ=0
    g34: LineSegment StartX=-28.4217 StartY=14.5789 StartZ=0 EndX=-28.1786 EndY=15.9576 EndZ=0
    g35: LineSegment StartX=-28.1786 StartY=15.9576 StartZ=0 EndX=-21.285 EndY=14.7421 EndZ=0
    g36: LineSegment StartX=-21.285 StartY=14.7421 StartZ=0 EndX=-14.3913 EndY=13.5265 EndZ=0
    g37: LineSegment StartX=-14.3913 StartY=13.5265 StartZ=0 EndX=-14.6344 EndY=12.1478 EndZ=0
    g38: LineSegment StartX=-14.6344 StartY=12.1478 StartZ=0 EndX=-13.3542 EndY=11.9221 EndZ=0
    g39: LineSegment StartX=-13.3542 StartY=11.9221 StartZ=0 EndX=-15.0859 EndY=9.58731 EndZ=0
    g40: LineSegment StartX=-15.0859 StartY=9.58731 StartZ=0 EndX=-21.9796 EndY=10.8028 EndZ=0
    g41: LineSegment StartX=-21.9796 StartY=10.8028 StartZ=0 EndX=-28.8732 EndY=12.0184 EndZ=0
    g42: LineSegment StartX=-28.8732 StartY=12.0184 StartZ=0 EndX=-29.702 EndY=14.8046 EndZ=0
    g43: LineSegment StartX=-6.62474 StartY=9.21789 StartZ=0 EndX=-8.14638 EndY=11.6947 EndZ=0
    g44: LineSegment StartX=-8.14638 StartY=11.6947 StartZ=0 EndX=-6.85133 EndY=11.808 EndZ=0
    g45: LineSegment StartX=-6.85133 StartY=11.808 StartZ=0 EndX=-6.97336 EndY=13.2027 EndZ=0
    g46: LineSegment StartX=-6.97336 StartY=13.2027 StartZ=0 EndX=0 EndY=13.8128 EndZ=0
    g47: LineSegment StartX=0 StartY=13.8128 StartZ=0 EndX=6.97336 EndY=14.4228 EndZ=0
    g48: LineSegment StartX=6.97336 StartY=14.4228 StartZ=0 EndX=7.0954 EndY=13.0282 EndZ=0
    g49: LineSegment StartX=7.0954 StartY=13.0282 StartZ=0 EndX=8.39044 EndY=13.1415 EndZ=0
    g50: LineSegment StartX=8.39044 StartY=13.1415 StartZ=0 EndX=7.32199 EndY=10.4381 EndZ=0
    g51: LineSegment StartX=7.32199 StartY=10.4381 StartZ=0 EndX=0.348623 EndY=9.82798 EndZ=0
    g52: LineSegment StartX=0.348623 StartY=9.82798 StartZ=0 EndX=-6.62474 EndY=9.21789 EndZ=0
    g53: LineSegment StartX=15.5905 StartY=12.2711 StartZ=0 EndX=13.4796 EndY=14.2697 EndZ=0
    g54: LineSegment StartX=13.4796 StartY=14.2697 StartZ=0 EndX=14.7012 EndY=14.7144 EndZ=0
    g55: LineSegment StartX=14.7012 StartY=14.7144 StartZ=0 EndX=14.2224 EndY=16.0299 EndZ=0
    g56: LineSegment StartX=14.2224 StartY=16.0299 StartZ=0 EndX=20.8002 EndY=18.4241 EndZ=0
    g57: LineSegment StartX=20.8002 StartY=18.4241 StartZ=0 EndX=27.3781 EndY=20.8182 EndZ=0
    g58: LineSegment StartX=27.3781 StartY=20.8182 StartZ=0 EndX=27.8569 EndY=19.5026 EndZ=0
    g59: LineSegment StartX=27.8569 StartY=19.5026 StartZ=0 EndX=29.0785 EndY=19.9473 EndZ=0
    g60: LineSegment StartX=29.0785 StartY=19.9473 StartZ=0 EndX=28.7462 EndY=17.0594 EndZ=0
    g61: LineSegment StartX=28.7462 StartY=17.0594 StartZ=0 EndX=22.1683 EndY=14.6653 EndZ=0
    g62: LineSegment StartX=22.1683 StartY=14.6653 StartZ=0 EndX=15.5905 EndY=12.2711 EndZ=0
    g63: LineSegment StartX=33.7023 StartY=22.3542 StartZ=0 EndX=34.7672 EndY=23.0999 EndZ=0
    g64: LineSegment StartX=34.7672 StartY=23.0999 StartZ=0 EndX=33.9642 EndY=24.2467 EndZ=0
    g65: LineSegment StartX=33.9642 StartY=24.2467 StartZ=0 EndX=39.6982 EndY=28.2617 EndZ=0
    g66: LineSegment StartX=39.6982 StartY=28.2617 StartZ=0 EndX=45.4323 EndY=32.2768 EndZ=0
    g67: LineSegment StartX=45.4323 StartY=32.2768 StartZ=0 EndX=46.2353 EndY=31.13 EndZ=0
    g68: LineSegment StartX=46.2353 StartY=31.13 StartZ=0 EndX=47.3002 EndY=31.8756 EndZ=0
    g69: LineSegment StartX=47.7266 StartY=29.0002 StartZ=0 EndX=41.9925 EndY=24.9851 EndZ=0
    g70: LineSegment StartX=41.9925 StartY=24.9851 StartZ=0 EndX=36.2585 EndY=20.9701 EndZ=0
    g71: LineSegment StartX=-49.6388 StartY=20.4818 StartZ=0 EndX=-43.2946 EndY=17.5235 EndZ=0
    g72: LineSegment StartX=-43.2946 StartY=17.5235 StartZ=0 EndX=-36.9505 EndY=14.5651 EndZ=0
    g73: LineSegment StartX=48.7915 StartY=29.7458 StartZ=0 EndX=47.7266 EndY=29.0002 EndZ=0
    g74: LineSegment StartX=36.2585 StartY=20.9701 StartZ=0 EndX=35.1936 EndY=20.2244 EndZ=0
    g75: LineSegment StartX=47.3002 StartY=31.8756 StartZ=0 EndX=47.7266 EndY=29.0002 EndZ=0
    g76: LineSegment StartX=33.7023 StartY=22.3542 StartZ=0 EndX=36.2585 EndY=20.9701 EndZ=0
    g77: LineSegment StartX=29.9678 StartY=17.5041 StartZ=0 EndX=28.7462 EndY=17.0594 EndZ=0
    g78: LineSegment StartX=15.5905 StartY=12.2711 StartZ=0 EndX=14.3689 EndY=11.8265 EndZ=0
    g79: LineSegment StartX=-6.62474 StartY=9.21789 StartZ=0 EndX=-7.91979 EndY=9.10459 EndZ=0
    g80: LineSegment StartX=7.32199 StartY=10.4381 StartZ=0 EndX=8.61704 EndY=10.5514 EndZ=0
    g81: LineSegment StartX=-30.1535 StartY=12.2441 StartZ=0 EndX=-28.8732 EndY=12.0184 EndZ=0
    g82: LineSegment StartX=-15.0859 StartY=9.58731 StartZ=0 EndX=-13.8057 EndY=9.36157 EndZ=0
    g83: LineSegment StartX=-50.817 StartY=21.0312 StartZ=0 EndX=-49.6388 EndY=20.4818 EndZ=0
    g84: LineSegment StartX=-36.9505 StartY=14.5651 StartZ=0 EndX=-35.7723 EndY=14.0157 EndZ=0
  constraints (235):
    c: PointOnObject(g0,g-3)
    c: PointOnObject(g0,g-5)
    c: PointOnObject(g1,g-5)
    c: PointOnObject(g1,g-3)
    c: Coincident(g2,g-4)
    c: PointOnObject(g2,g-5)
    c: PointOnObject(g3,g-4)
    c: PointOnObject(g3,g-5)
    c: PointOnObject(g4,g-5)
    c: PointOnObject(g4,g-4)
    c: PointOnObject(g5,g-6)
    c: PointOnObject(g5,g-8)
    c: PointOnObject(g6,g-8)
    c: PointOnObject(g6,g-6)
    c: Coincident(g7,g-7)
    c: PointOnObject(g7,g-8)
    c: PointOnObject(g8,g-8)
    c: PointOnObject(g8,g-7)
    c: PointOnObject(g9,g-7)
    c: PointOnObject(g9,g-8)
    c: PointOnObject(g10,g-9)
    c: PointOnObject(g10,g-11)
    c: PointOnObject(g11,g-11)
    c: PointOnObject(g11,g-9)
    c: Coincident(g12,g-10)
    c: PointOnObject(g12,g-11)
    c: PointOnObject(g13,g-11)
    c: PointOnObject(g13,g-10)
    c: PointOnObject(g14,g-10)
    c: PointOnObject(g14,g-11)
    c: PointOnObject(g15,g-12)
    c: PointOnObject(g15,g-14)
    c: PointOnObject(g16,g-14)
    c: PointOnObject(g16,g-12)
    c: Coincident(g17,g-14)
    c: PointOnObject(g17,g-12)
    c: PointOnObject(g18,g-12)
    c: PointOnObject(g18,g-13)
    c: PointOnObject(g19,g-13)
    c: PointOnObject(g19,g-12)
    c: PointOnObject(g20,g-17)
    c: PointOnObject(g20,g-15)
    c: PointOnObject(g21,g-15)
    c: PointOnObject(g21,g-17)
    c: Coincident(g22,g-16)
    c: PointOnObject(g22,g-17)
    c: PointOnObject(g23,g-16)
    c: PointOnObject(g23,g-17)
    c: PointOnObject(g24,g-17)
    c: PointOnObject(g24,g-16)
    c: Perpendicular(g-16,g23)
    c: Perpendicular(g-15,g22)
    c: Perpendicular(g-15,g21)
    c: Perpendicular(g-17,g20)
    c: Perpendicular(g-12,g19)
    c: Perpendicular(g-13,g18)
    c: Perpendicular(g-14,g17)
    c: Perpendicular(g-14,g16)
    c: Perpendicular(g-12,g15)
    c: Perpendicular(g-11,g14)
    c: Perpendicular(g-10,g13)
    c: Perpendicular(g-9,g12)
    c: Perpendicular(g-9,g11)
    c: Perpendicular(g-11,g10)
    c: Perpendicular(g-8,g9)
    c: Perpendicular(g-7,g8)
    c: Perpendicular(g-6,g7)
    c: Perpendicular(g-6,g6)
    c: Perpendicular(g-8,g5)
    c: Perpendicular(g-5,g4)
    c: Perpendicular(g-4,g3)
    c: Perpendicular(g-3,g2)
    c: Perpendicular(g-5,g0)
    c: Perpendicular(g-3,g1)
    c: Coincident(g1,g25)
    c: Coincident(g25,g2)
    c: Coincident(g25,g26)
    c: Coincident(g26,g3)
    c: Coincident(g26,g27)
    c: Coincident(g27,g28)
    c: Coincident(g28,g29)
    c: Coincident(g30,g31)
    c: Coincident(g31,g32)
    c: Coincident(g32,g25)
    c: Coincident(g33,g34)
    c: Coincident(g34,g6)
    c: Coincident(g34,g35)
    c: Coincident(g35,g7)
    c: Coincident(g35,g36)
    c: Coincident(g36,g8)
    c: Coincident(g36,g37)
    c: Coincident(g37,g38)
    c: Coincident(g38,g39)
    c: Coincident(g40,g7)
    c: Coincident(g40,g41)
    c: Coincident(g42,g33)
    c: Coincident(g43,g44)
    c: Coincident(g44,g45)
    c: Coincident(g45,g11)
    c: Coincident(g45,g46)
    c: Coincident(g46,g12)
    c: Coincident(g46,g47)
    c: Coincident(g47,g13)
    c: Coincident(g47,g48)
    c: Coincident(g48,g49)
    c: Coincident(g49,g50)
    c: Coincident(g51,g12)
    c: Coincident(g51,g52)
    c: Coincident(g53,g54)
    c: Coincident(g54,g55)
    c: Coincident(g55,g16)
    c: Coincident(g55,g56)
    c: Coincident(g56,g17)
    c: Coincident(g56,g57)
    c: Coincident(g57,g18)
    c: Coincident(g57,g58)
    c: Coincident(g58,g59)
    c: Coincident(g59,g60)
    c: Coincident(g61,g17)
    c: Coincident(g61,g62)
    c: Coincident(g63,g64)
    c: Coincident(g64,g21)
    c: Coincident(g64,g65)
    c: Coincident(g65,g22)
    c: Coincident(g65,g66)
    c: Coincident(g66,g23)
    c: Coincident(g66,g67)
    c: Coincident(g67,g68)
    c: Coincident(g69,g22)
    c: Coincident(g69,g70)
    c: Distance(g67) = 1.4
    c: Distance(g64) = 1.4
    c: Distance(g58) = 1.4
    c: Distance(g55) = 1.4
    c: Distance(g48) = 1.4
    c: Distance(g45) = 1.4
    c: Distance(g37) = 1.4
    c: Distance(g34) = 1.4
    c: Distance(g27) = 1.4
    c: Distance(g32) = 1.4
    c: Distance(g25,g26) = 14
    c: Distance(g34,g36) = 14
    c: Distance(g45,g47) = 14
    c: Distance(g55,g57) = 14
    c: Distance(g64,g66) = 14
    c: Equal(g25,g26)
    c: Equal(g35,g36)
    c: Equal(g46,g47)
    c: Equal(g56,g57)
    c: Equal(g65,g66)
    c: Coincident(g71,g2)
    c: Coincident(g71,g72)
    c: Distance(g30,g0) = 1.4
    c: Distance(g28,g4) = 1.4
    c: Distance(g33,g5) = 1.4
    c: Distance(g38,g9) = 1.4
    c: Distance(g43,g10) = 1.4
    c: Distance(g49,g14) = 1.4
    c: Distance(g53,g15) = 1.4
    c: Distance(g59,g19) = 1.4
    c: Distance(g63,g20) = 1.4
    c: Distance(g68,g24) = 1.4
    c: Distance(g24,g20) = 16.6
    c: Distance(g63,g21) = 2.6
    c: Distance(g63,g20) = 2.6
    c: Coincident(g73,g24)
    c: Coincident(g73,g69)
    c: Coincident(g74,g70)
    c: Coincident(g74,g20)
    c: Equal(g74,g73)
    c: Coincident(g70,g21)
    c: Perpendicular(g-17,g24)
    c: Coincident(g69,g23)
    c: Coincident(g75,g68)
    c: Coincident(g75,g69)
    c: Distance(g68,g24) = 2.6
    c: Distance(g67,g69) = 2.6
    c: Coincident(g76,g63)
    c: Coincident(g76,g70)
    c: Distance(g54,g16) = 2.6
    c: Distance(g58,g18) = 2.6
    c: Coincident(g61,g18)
    c: Coincident(g62,g16)
    c: Coincident(g77,g19)
    c: Coincident(g77,g61)
    c: Coincident(g78,g62)
    c: Coincident(g78,g15)
    c: Coincident(g60,g61)
    c: Distance(g59,g19) = 2.6
    c: Coincident(g53,g62)
    c: Equal(g78,g77)
    c: Distance(g15,g19) = 16.6
    c: Distance(g15,g53) = 2.6
    c: Coincident(g52,g43)
    c: Coincident(g52,g11)
    c: Coincident(g50,g13)
    c: Coincident(g50,g51)
    c: Distance(g49,g14) = 2.6
    c: Distance(g48,g50) = 2.6
    c: Distance(g14,g10) = 16.6
    c: Coincident(g79,g43)
    c: Coincident(g79,g10)
    c: Coincident(g80,g50)
    c: Coincident(g80,g14)
    c: Equal(g80,g79)
    c: Distance(g44,g43) = 2.6
    c: Distance(g43,g10) = 2.6
    c: Coincident(g8,g40)
    c: Coincident(g8,g39)
    c: Coincident(g41,g6)
    c: Coincident(g41,g42)
    c: Coincident(g81,g5)
    c: Coincident(g81,g41)
    c: Coincident(g82,g39)
    c: Coincident(g82,g9)
    c: Equal(g81,g82)
    c: Distance(g5,g9) = 16.6
    c: Distance(g38,g9) = 2.6
    c: Distance(g37,g39) = 2.6
    c: Distance(g33,g41) = 2.6
    c: Distance(g33,g5) = 2.6
    c: Coincident(g71,g1)
    c: Coincident(g71,g30)
    c: Coincident(g3,g72)
    c: Coincident(g3,g29)
    c: Coincident(g83,g0)
    c: Coincident(g83,g30)
    c: Coincident(g84,g29)
    c: Coincident(g84,g4)
    c: Distance(g30,g0) = 2.6
    c: Distance(g31,g30) = 2.6
    c: Distance(g0,g4) = 16.6
    c: Distance(g4,g28) = 2.6
    c: Distance(g27,g29) = 2.6
    c: Equal(g84,g83)
FEATURE [PartDesign::Pocket] Pocket002  label="PMX Sockets"
  BaseFeature = -> Pad004
  Direction = (-1,2e-16,-3e-16)
  Length = 14
  Length2 = 100
  Midplane = true
  Placement = pos=(0,0,0) rot=(0.57735,0.57735,0.57735;2.0944rad)
  Profile = -> Sketch007
  Type = 0
FEATURE [Sketcher::SketchObject] Sketch008
  ExternalGeometry = -> [Sketch007]
  FullyConstrained = true
  MapMode = 5
  Placement = pos=(0,0,0) rot=(0.57735,0.57735,0.57735;2.0944rad)
  Support = -> [YZ_Plane001]
  sketch-geometry (20):
    g0: LineSegment StartX=-35.7672 StartY=17.1028 StartZ=0 EndX=-36.1898 EndY=16.1965 EndZ=0
    g1: LineSegment StartX=-36.1898 StartY=16.1965 StartZ=0 EndX=-48.8781 EndY=22.1132 EndZ=0
    g2: LineSegment StartX=-48.8781 StartY=22.1132 StartZ=0 EndX=-48.4555 EndY=23.0195 EndZ=0
    g3: LineSegment StartX=-48.4555 StartY=23.0195 StartZ=0 EndX=-35.7672 EndY=17.1028 EndZ=0
    g4: LineSegment StartX=-28.387 StartY=14.7758 StartZ=0 EndX=-28.5607 EndY=13.791 EndZ=0
    g5: LineSegment StartX=-28.5607 StartY=13.791 StartZ=0 EndX=-14.7734 EndY=11.36 EndZ=0
    g6: LineSegment StartX=-14.7734 StartY=11.36 StartZ=0 EndX=-14.5997 EndY=12.3448 EndZ=0
    g7: LineSegment StartX=-14.5997 StartY=12.3448 StartZ=0 EndX=-28.387 EndY=14.7758 EndZ=0
    g8: LineSegment StartX=-6.86876 StartY=12.0072 StartZ=0 EndX=-6.78161 EndY=11.011 EndZ=0
    g9: LineSegment StartX=-6.78161 StartY=11.011 StartZ=0 EndX=7.16511 EndY=12.2312 EndZ=0
    g10: LineSegment StartX=7.16511 StartY=12.2312 StartZ=0 EndX=7.07796 EndY=13.2274 EndZ=0
    g11: LineSegment StartX=7.07796 StartY=13.2274 StartZ=0 EndX=-6.86876 EndY=12.0072 EndZ=0
    g12: LineSegment StartX=14.6328 StartY=14.9023 StartZ=0 EndX=14.9748 EndY=13.9626 EndZ=0
    g13: LineSegment StartX=14.9748 StartY=13.9626 StartZ=0 EndX=28.1305 EndY=18.7509 EndZ=0
    g14: LineSegment StartX=28.1305 StartY=18.7509 StartZ=0 EndX=27.7885 EndY=19.6906 EndZ=0
    g15: LineSegment StartX=27.7885 StartY=19.6906 StartZ=0 EndX=14.6328 EndY=14.9023 EndZ=0
    g16: LineSegment StartX=34.6525 StartY=23.2637 StartZ=0 EndX=35.226 EndY=22.4446 EndZ=0
    g17: LineSegment StartX=35.226 StartY=22.4446 StartZ=0 EndX=46.6942 EndY=30.4746 EndZ=0
    g18: LineSegment StartX=46.6942 StartY=30.4746 StartZ=0 EndX=46.1206 EndY=31.2938 EndZ=0
    g19: LineSegment StartX=46.1206 StartY=31.2938 StartZ=0 EndX=34.6525 EndY=23.2637 EndZ=0
  constraints (60):
    c: Coincident(g0,g1)
    c: Coincident(g2,g1)
    c: Distance(g0,g-20) = 1.8
    c: Distance(g1,g-19) = 1.8
    c: Distance(g-22,g2) = 0.2
    c: Distance(g2,g-22) = 1.2
    c: Distance(g-22,g1) = 0.8
    c: Distance(g-21,g0) = 0.2
    c: Distance(g-21,g0) = 0.8
    c: Distance(g0,g-21) = 1.2
    c: Coincident(g3,g2)
    c: Coincident(g3,g0)
    c: Coincident(g4,g5)
    c: Coincident(g5,g6)
    c: Coincident(g6,g7)
    c: Coincident(g7,g4)
    c: Coincident(g8,g9)
    c: Coincident(g9,g10)
    c: Coincident(g10,g11)
    c: Coincident(g11,g8)
    c: Coincident(g12,g13)
    c: Coincident(g13,g14)
    c: Coincident(g14,g15)
    c: Coincident(g15,g12)
    c: Coincident(g16,g17)
    c: Coincident(g17,g18)
    c: Coincident(g18,g19)
    c: Coincident(g19,g16)
    c: Distance(g-6,g4) = 0.2
    c: Distance(g-6,g4) = 1.2
    c: Distance(g4,g-5) = 1.8
    c: Distance(g4,g-6) = 0.8
    c: Distance(g6,g-3) = 1.2
    c: Distance(g6,g-3) = 0.2
    c: Distance(g5,g-4) = 1.8
    c: Distance(g-3,g5) = 0.8
    c: Distance(g8,g-10) = 1.2
    c: Distance(g8,g-10) = 0.2
    c: Distance(g8,g-9) = 1.8
    c: Distance(g8,g-10) = 0.8
    c: Distance(g10,g-7) = 1.2
    c: Distance(g10,g-7) = 0.2
    c: Distance(g9,g-8) = 1.8
    c: Distance(g-7,g9) = 0.8
    c: Distance(g12,g-12) = 1.2
    c: Distance(g12,g-12) = 0.2
    c: Distance(g12,g-13) = 1.8
    c: Distance(g12,g-12) = 0.8
    c: Distance(g14,g-11) = 1.2
    c: Distance(g14,g-11) = 0.2
    c: Distance(g13,g-14) = 1.8
    c: Distance(g13,g-11) = 0.8
    c: Distance(g18,g-17) = 0.2
    c: Distance(g17,g-17) = 0.8
    c: Distance(g17,g-18) = 1.8
    c: Distance(g18,g-17) = 1.2
    c: Distance(g-15,g16) = 1.8
    c: Distance(g16,g-16) = 0.8
    c: Distance(g16,g-16) = 0.2
    c: Distance(g16,g-16) = 1.2
FEATURE [PartDesign::Pocket] Pocket003  label="PChoc Sockets"
  BaseFeature = -> Pocket002
  Direction = (-1,2e-16,-3e-16)
  Length = 14.6
  Length2 = 100
  Midplane = true
  Placement = pos=(0,0,0) rot=(0.57735,0.57735,0.57735;2.0944rad)
  Profile = -> Sketch008
  Type = 0
FEATURE [Sketcher::SketchObject] Sketch009
  ExternalGeometry = -> [Sketch006]
  FullyConstrained = true
  MapMode = 5
  Placement = pos=(0,0,0) rot=(0.57735,0.57735,0.57735;2.0944rad)
  Support = -> [YZ_Plane001]
  expr: Constraints[24] = <<Spreadsheet>>.Wiring
  expr: Constraints[25] = <<Spreadsheet>>.Wiring
  expr: Constraints[26] = <<Spreadsheet>>.Wiring
  expr: Constraints[27] = <<Spreadsheet>>.Wiring
  sketch-geometry (12):
    g0: LineSegment StartX=-11.9293 StartY=13.0924 StartZ=0 EndX=-9.46385 EndY=12.9848 EndZ=0
    g1: LineSegment StartX=-9.46385 StartY=12.9848 StartZ=0 EndX=-8.59231 EndY=3.02283 EndZ=0
    g2: LineSegment StartX=-8.59231 StartY=3.02283 StartZ=0 EndX=-8.59231 EndY=0 EndZ=0
    g3: LineSegment StartX=-8.59231 StartY=0 StartZ=0 EndX=-13.6658 EndY=0 EndZ=0
    g4: LineSegment StartX=-13.6658 StartY=0 StartZ=0 EndX=-13.6658 EndY=3.24435 EndZ=0
    g5: LineSegment StartX=-13.6658 StartY=3.24435 StartZ=0 EndX=-11.9293 EndY=13.0924 EndZ=0
    g6: LineSegment StartX=9.46385 StartY=14.6407 StartZ=0 EndX=11.8732 EndY=15.1749 EndZ=0
    g7: LineSegment StartX=11.8732 StartY=15.1749 StartZ=0 EndX=15.2933 EndY=5.77794 EndZ=0
    g8: LineSegment StartX=15.2933 StartY=5.77794 StartZ=0 EndX=15.2933 EndY=0 EndZ=0
    g9: LineSegment StartX=15.2933 StartY=0 StartZ=0 EndX=10.3354 EndY=0 EndZ=0
    g10: LineSegment StartX=10.3354 StartY=0 StartZ=0 EndX=10.3354 EndY=4.67879 EndZ=0
    g11: LineSegment StartX=10.3354 StartY=4.67879 StartZ=0 EndX=9.46385 EndY=14.6407 EndZ=0
  constraints (32):
    c: Coincident(g0,g-6)
    c: Coincident(g0,g-6)
    c: Coincident(g0,g1)
    c: Coincident(g1,g2)
    c: PointOnObject(g2,g-1)
    c: Vertical(g2)
    c: Coincident(g2,g3)
    c: Horizontal(g3)
    c: Coincident(g3,g4)
    c: Vertical(g4)
    c: Coincident(g4,g5)
    c: Coincident(g5,g0)
    c: Coincident(g-4,g6)
    c: Coincident(g6,g-4)
    c: Coincident(g6,g7)
    c: Coincident(g7,g8)
    c: PointOnObject(g8,g-1)
    c: Vertical(g8)
    c: Coincident(g8,g9)
    c: Horizontal(g9)
    c: Coincident(g9,g10)
    c: Vertical(g10)
    c: Coincident(g10,g11)
    c: Coincident(g11,g6)
    c: Distance(g-3,g7) = 6
    c: Distance(g-3,g10) = 6
    c: Distance(g-5,g1) = 6
    c: Distance(g-5,g4) = 6
    c: Equal(g5,g1)
    c: Equal(g1,g11)
    c: Equal(g11,g7)
    c: Distance(g5) = 10
FEATURE [PartDesign::Pad] Pad005  label="PInner Legs"
  BaseFeature = -> Pocket003
  Direction = (1,-2e-16,3e-16)
  Length = 4.1
  Length2 = 9.5
  Placement = pos=(0,0,0) rot=(0.57735,0.57735,0.57735;2.0944rad)
  Profile = -> Sketch009
  Type = 4
  expr: Length = <<Spreadsheet>>.ScrewD / 2 + 2mm
FEATURE [Sketcher::SketchObject] Sketch010
  ExternalGeometry = -> [Sketch006]
  FullyConstrained = true
  MapMode = 5
  Placement = pos=(0,0,0) rot=(0.57735,0.57735,0.57735;2.0944rad)
  Support = -> [YZ_Plane001]
  expr: Constraints[11] = <<Spreadsheet>>.Wiring + 4mm
  expr: Constraints[12] = <<Spreadsheet>>.Wiring
  expr: Constraints[13] = <<Spreadsheet>>.Wiring
  expr: Constraints[14] = <<Spreadsheet>>.Wiring
  expr: Constraints[15] = <<Spreadsheet>>.Wiring
  expr: Constraints[76] = <<Spreadsheet>>.ArchLength
  expr: Constraints[77] = <<Spreadsheet>>.ArchLength
  expr: Constraints[78] = <<Spreadsheet>>.ArchLength * 2 - 10mm
  sketch-geometry (32):
    g0: LineSegment StartX=-37.2205 StartY=8.07076 StartZ=0 EndX=-32.9942 EndY=17.1338 EndZ=0
    g1: LineSegment StartX=-32.9942 StartY=17.1338 StartZ=0 EndX=-30.6407 EndY=16.3917 EndZ=0
    g2: LineSegment StartX=-30.6407 StartY=16.3917 StartZ=0 EndX=-32.3772 EndY=6.54366 EndZ=0
    g3: LineSegment StartX=33.1475 StartY=12.2763 StartZ=0 EndX=29.7273 EndY=21.6733 EndZ=0
    g4: LineSegment StartX=29.7273 StartY=21.6733 StartZ=0 EndX=31.9163 EndY=22.8128 EndZ=0
    g5: LineSegment StartX=31.9163 StartY=22.8128 StartZ=0 EndX=37.6521 EndY=14.6212 EndZ=0
    g6: LineSegment StartX=37.6521 StartY=14.6212 StartZ=0 EndX=42.2621 EndY=8.03739 EndZ=0
    g7: LineSegment StartX=42.2621 StartY=8.03739 StartZ=0 EndX=42.2621 EndY=0 EndZ=0
    g8: LineSegment StartX=-37.2205 StartY=8.07076 StartZ=0 EndX=-39.0097 EndY=4.23371 EndZ=0
    g9: LineSegment StartX=-39.0097 StartY=4.23371 StartZ=0 EndX=-39.0097 EndY=0 EndZ=0
    g10: LineSegment StartX=-32.3772 StartY=6.54366 StartZ=0 EndX=-35 EndY=0 EndZ=0
    g11: LineSegment StartX=-35 StartY=0 StartZ=0 EndX=-45 EndY=0 EndZ=0
    g12: LineSegment StartX=-45 StartY=0 StartZ=0 EndX=-45 EndY=3 EndZ=0
    g13: LineSegment StartX=-45 StartY=3 StartZ=0 EndX=-40 EndY=3 EndZ=0
    g14-g17: Circle x4 (B-spline internal-alignment scaffolding for g18; pole/knot coordinates omitted)
    g18: BSplineCurve PolesCount=4 KnotsCount=2 Degree=3 IsPeriodic=0
    g19: GeomPoint X=-37.2205 Y=8.07076 Z=0
    g20: GeomPoint X=-45 Y=3 Z=0
    g21: LineSegment StartX=33.1475 StartY=12.2763 StartZ=0 EndX=35 EndY=0 EndZ=0
    g22: LineSegment StartX=35 StartY=0 StartZ=0 EndX=45 EndY=0 EndZ=0
    g23: LineSegment StartX=45 StartY=0 StartZ=0 EndX=45 EndY=3 EndZ=0
    g24: LineSegment StartX=45 StartY=3 StartZ=0 EndX=40 EndY=3 EndZ=0
    g25-g28: Circle x4 (B-spline internal-alignment scaffolding for g29; pole/knot coordinates omitted)
    g29: BSplineCurve PolesCount=4 KnotsCount=2 Degree=3 IsPeriodic=0
    g30: GeomPoint X=37.6521 Y=14.6212 Z=0
    g31: GeomPoint X=45 Y=3 Z=0
  constraints (74):
    c: Coincident(g0,g-5)
    c: Coincident(g0,g1)
    c: Coincident(g1,g-5)
    c: Coincident(g1,g2)
    c: Coincident(g3,g-4)
    c: Coincident(g3,g4)
    c: Coincident(g4,g-4)
    c: Coincident(g4,g5)
    c: Equal(g2,g0)
    c: Equal(g0,g3)
    c: Equal(g3,g5)
    c: Distance(g0) = 10
    c: Distance(g-6,g0) = 6
    c: Distance(g-6,g2) = 6
    c: Distance(g-3,g3) = 6
    c: Distance(g-3,g5) = 6
    c: Coincident(g5,g6)
    c: Coincident(g6,g7)
    c: Vertical(g7)
    c: Coincident(g0,g8)
    c: Coincident(g8,g9)
    c: Vertical(g9)
    c: Parallel(g6,g5)
    c: Parallel(g0,g8)
    c: Equal(g8,g9)
    c: Equal(g7,g6)
    c: PointOnObject(g7,g-1)
    c: PointOnObject(g9,g-1)
    c: Coincident(g2,g10)
    c: PointOnObject(g10,g-1)
    c: Coincident(g10,g11)
    c: PointOnObject(g11,g-1)
    c: Coincident(g11,g12)
    c: Vertical(g12)
    c: Coincident(g13,g12)
    c: Horizontal(g13)
    c: DistanceY(g12,g12) = 3
    c: Coincident(g18,g0)
    c: Weight(g14) = 1
    c: Equal(g14,g15)
    c: Coincident(g15,g8)
    c: Equal(g14,g16)
    c: Coincident(g16,g13)
    c: Equal(g14,g17)
    c: Coincident(g18,g12)
    c: InternalAlignment(g14-g17 -> g18) x4
    c: InternalAlignment(g19,g18)
    c: InternalAlignment(g20,g18)
    c: Coincident(g3,g21)
    c: PointOnObject(g21,g-1)
    c: Coincident(g21,g22)
    c: Horizontal(g22)
    c: Coincident(g22,g23)
    c: Vertical(g23)
    c: DistanceY(g23,g23) = 3
    c: Coincident(g24,g23)
    c: Horizontal(g24)
    c: Coincident(g29,g5)
    c: Weight(g25) = 1
    c: Equal(g25,g26)
    c: Coincident(g26,g6)
    c: Equal(g25,g27)
    c: Coincident(g27,g24)
    c: Equal(g25,g28)
    c: Coincident(g29,g23)
    c: InternalAlignment(g25-g28 -> g29) x4
    c: InternalAlignment(g30,g29)
    c: InternalAlignment(g31,g29)
    c: Equal(g22,g11)
    c: DistanceX(g11,g11) = 10
    c: DistanceX(g-7,g22) = 45
    c: DistanceX(g11,g-7) = 45
    c: DistanceX(g13,g24) = 80
    c: Equal(g24,g13)
FEATURE [PartDesign::Pad] Pad006  label="POuter Legs"
  BaseFeature = -> Pad005
  Direction = (1,-2e-16,3e-16)
  Length = 9.5
  Length2 = 100
  Placement = pos=(0,0,0) rot=(0.57735,0.57735,0.57735;2.0944rad)
  Profile = -> Sketch010
  Reversed = true
  Type = 0
FEATURE [Sketcher::SketchObject] Sketch011
  ExternalGeometry = -> [Sketch010]
  FullyConstrained = true
  MapMode = 5
  Support = -> [XY_Plane001]
  expr: Constraints[25] = <<Spreadsheet>>.NutR
  expr: Constraints[26] = <<Spreadsheet>>.NutR
  expr: Constraints[27] = <<Spreadsheet>>.ScrewD
  expr: Constraints[40] = <<Spreadsheet>>.ScrewD
  expr: Constraints[54] = <<Spreadsheet>>.NutR
  expr: Constraints[55] = <<Spreadsheet>>.NutR
  sketch-geometry (22):
    g0: LineSegment StartX=9.8e-15 StartY=45 StartZ=0 EndX=-9.5 EndY=45 EndZ=0
    g1: LineSegment StartX=-9.5 StartY=45 StartZ=0 EndX=-9.5 EndY=55 EndZ=0
    g2: LineSegment StartX=-9.5 StartY=55 StartZ=0 EndX=4.5 EndY=55 EndZ=0
    g3: ArcOfCircle CenterX=4.5 CenterY=50 CenterZ=0 NormalX=0 NormalY=0 NormalZ=1 AngleXU=0 Radius=5 StartAngle=5.38688 EndAngle=7.85398
    g4: LineSegment StartX=7.6225 StartY=46.0949 StartZ=0 EndX=9.8e-15 EndY=40 EndZ=0
    g5: LineSegment StartX=9.8e-15 StartY=40 StartZ=0 EndX=9.8e-15 EndY=45 EndZ=0
    g6: Circle CenterX=0 CenterY=50 CenterZ=0 NormalX=0 NormalY=0 NormalZ=1 AngleXU=0 Radius=2.1
    g7: LineSegment StartX=0 StartY=50 StartZ=0 EndX=4.5 EndY=50 EndZ=0
    g8: LineSegment StartX=9.5 StartY=50 StartZ=0 EndX=9.5 EndY=55 EndZ=0
    g9: LineSegment StartX=-9.5 StartY=55 StartZ=0 EndX=0 EndY=50 EndZ=0
    g10: LineSegment StartX=0 StartY=50 StartZ=0 EndX=9.5 EndY=55 EndZ=0
    g11: LineSegment StartX=-9.8e-15 StartY=-40 StartZ=0 EndX=-9.8e-15 EndY=-45 EndZ=0
    g12: LineSegment StartX=-9.8e-15 StartY=-45 StartZ=0 EndX=-9.5 EndY=-45 EndZ=0
    g13: LineSegment StartX=-9.5 StartY=-45 StartZ=0 EndX=-9.5 EndY=-55 EndZ=0
    g14: LineSegment StartX=-9.5 StartY=-55 StartZ=0 EndX=4.5 EndY=-55 EndZ=0
    g15: ArcOfCircle CenterX=4.5 CenterY=-50 CenterZ=0 NormalX=0 NormalY=0 NormalZ=1 AngleXU=0 Radius=5 StartAngle=4.71239 EndAngle=7.17949
    g16: LineSegment StartX=7.6225 StartY=-46.0949 StartZ=0 EndX=-9.8e-15 EndY=-40 EndZ=0
    g17: Circle CenterX=0 CenterY=-50 CenterZ=0 NormalX=0 NormalY=0 NormalZ=1 AngleXU=0 Radius=2.1
    g18: LineSegment StartX=9.5 StartY=-50 StartZ=0 EndX=9.5 EndY=-55 EndZ=0
    g19: LineSegment StartX=9.5 StartY=-55 StartZ=0 EndX=0 EndY=-50 EndZ=0
    g20: LineSegment StartX=0 StartY=-50 StartZ=0 EndX=-9.5 EndY=-55 EndZ=0
    g21: LineSegment StartX=0 StartY=-50 StartZ=0 EndX=4.5 EndY=-50 EndZ=0
  constraints (58):
    c: Coincident(g0,g-3)
    c: Horizontal(g0)
    c: Coincident(g0,g1)
    c: Vertical(g1)
    c: Coincident(g1,g2)
    c: Horizontal(g2)
    c: Tangent(g2,g3) = 1.5708
    c: Tangent(g3,g4) = 1.5708
    c: Coincident(g4,g5)
    c: Coincident(g5,g0)
    c: Vertical(g5)
    c: PointOnObject(g6,g-2)
    c: Coincident(g7,g6)
    c: Coincident(g7,g3)
    c: PointOnObject(g8,g3)
    c: Vertical(g8)
    c: Horizontal(g2,g8)
    c: Coincident(g1,g9)
    c: Coincident(g9,g7)
    c: Coincident(g9,g10)
    c: Coincident(g10,g8)
    c: Horizontal(g7)
    c: Equal(g10,g9)
    c: DistanceX(g9,g8) = 19
    c: DistanceY(g5,g5) = 5
    c: DistanceY(g7,g9) = 5
    c: DistanceY(g0,g7) = 5
    c: Diameter(g6) = 4.2
    c: Tangent(g8,g3)
    c: Vertical(g11)
    c: Coincident(g11,g12)
    c: Horizontal(g12)
    c: Coincident(g12,g13)
    c: Vertical(g13)
    c: Coincident(g13,g14)
    c: Horizontal(g14)
    c: Tangent(g14,g15) = -1.5708
    c: Tangent(g15,g16) = -1.5708
    c: DistanceY(g11,g11) = 5
    c: PointOnObject(g17,g-2)
    c: Diameter(g17) = 4.2
    c: PointOnObject(g18,g15)
    c: Vertical(g18)
    c: Tangent(g18,g15)
    c: Coincident(g18,g19)
    c: Coincident(g19,g17)
    c: Coincident(g19,g20)
    c: Coincident(g20,g13)
    c: DistanceX(g20,g18) = 19
    c: Equal(g19,g20)
    c: Horizontal(g18,g14)
    c: Coincident(g21,g19)
    c: Coincident(g21,g15)
    c: Horizontal(g21)
    c: DistanceY(g20,g19) = 5
    c: DistanceY(g19,g12) = 5
    c: Coincident(g16,g11)
    c: Coincident(g11,g-4)
FEATURE [PartDesign::Pad] Pad007  label="PFeet"
  BaseFeature = -> Pad006
  Direction = (0,0,1)
  Length = 3
  Length2 = 100
  Placement = pos=(0,0,0) rot=(0.57735,0.57735,0.57735;2.0944rad)
  Profile = -> Sketch011
  Type = 0
FEATURE [PartDesign::Body] Body001  label="PinkieArch"
  Group = -> [Sketch006,Pad004,Sketch007,Pocket002,Sketch008,Pocket003,Sketch009,Pad005,Sketch010,Pad006,Sketch011,Pad007]
  Origin = -> Origin001
  Placement = pos=(30,-10,15) rot=(0,0,1;0rad)
  Tip = -> Pad007
  expr: .Placement.Base.y = <<OuterArch>>.Placement.Base.y
  expr: .Placement.Base.z = <<OuterArch>>.Placement.Base.z
